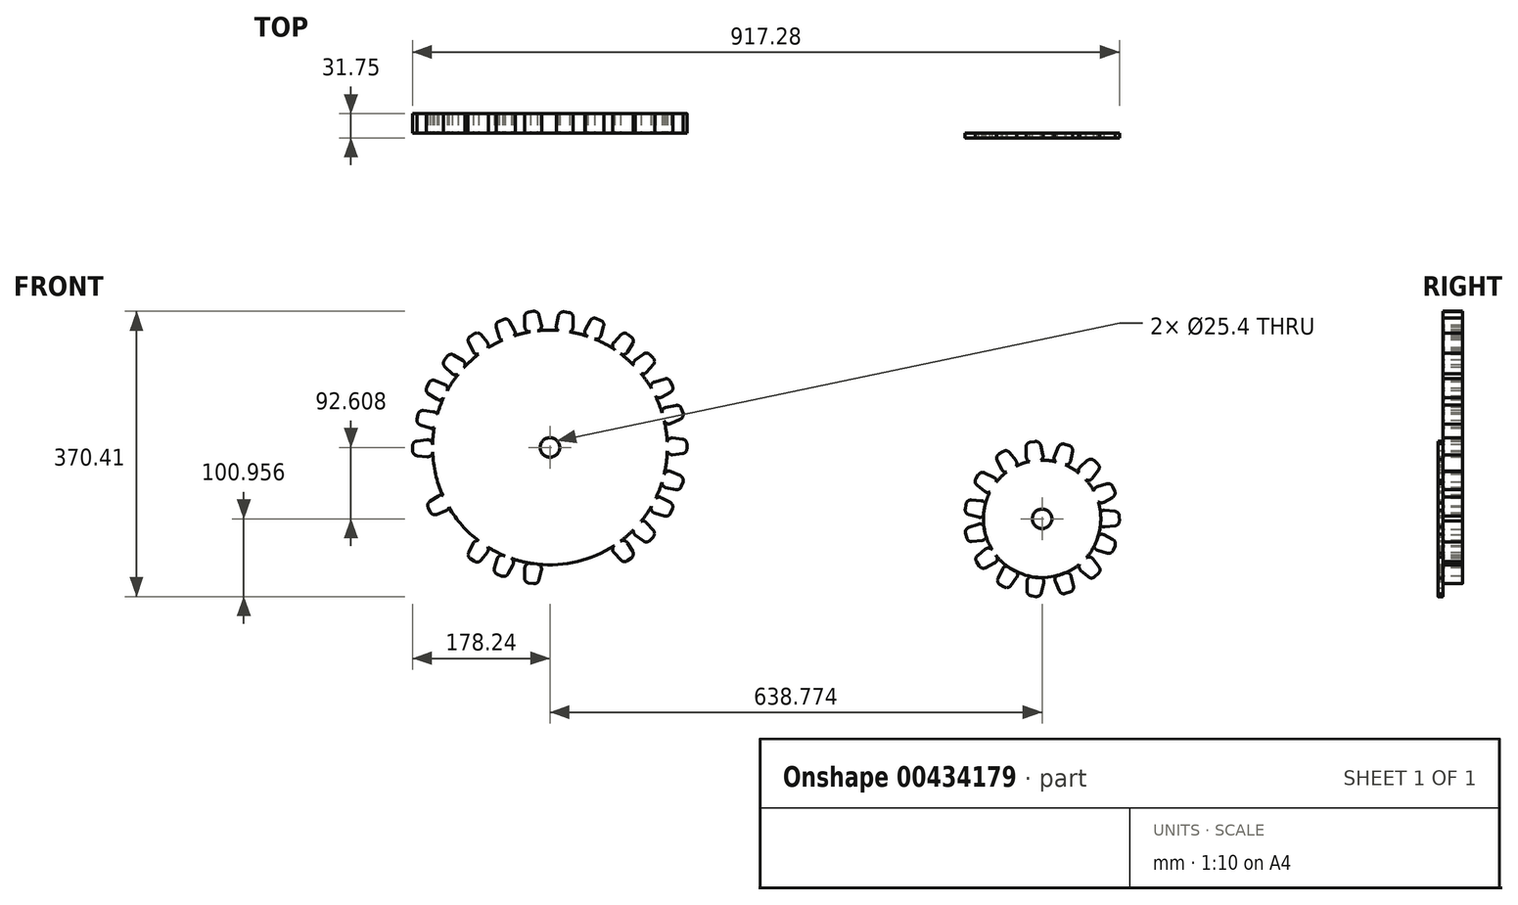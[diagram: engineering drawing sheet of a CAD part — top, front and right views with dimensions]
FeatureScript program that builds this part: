
annotation { "Feature Type Name" : "Feature", "Feature Type Description" : "" }
export const myFeature = defineFeature(function(context is Context, id is Id, definition is map)
    precondition{}
    {
        {
            var Q0;
            Q0=qCreatedBy(makeId("Front.planeOp"),FACE);
            var sketch = newSketch(context, id + "F0", { "sketchPlane" : qUnion([Q0])});
            skCircle(sketch, "E0", {"center": v(-249.13, 151.4) * mm, "radius": 152.4 * mm});
            skCircle(sketch, "E1", {"center": v(-249.13, 151.4) * mm, "radius": 12.7 * mm});
            skLineSegment(sketch, "E2", {"start": v(-197.07, 316) * mm, "end": v(-203.37, 304.29) * mm});
            skLineSegment(sketch, "E3", {"start": v(-199.76, 295.58) * mm, "end": v(-191.3, 292.4) * mm});
            skLineSegment(sketch, "E4", {"start": v(-183.23, 316.56) * mm, "end": v(-189.13, 318.9) * mm});
            skLineSegment(sketch, "E5.MirrorCS", {"start": v(-179.48, 308.88) * mm, "end": v(-183.09, 296.5) * mm});
            skArc(sketch, "E6.filletArc", {"start": v(-203.37, 304.29) * mm, "mid": v(-203.45, 299.15) * mm, "end": v(-199.76, 295.58) * mm});
            skArc(sketch, "E7.filletArc", {"start": v(-191.3, 292.4) * mm, "mid": v(-186.3, 292.65) * mm, "end": v(-183.09, 296.5) * mm});
            skArc(sketch, "E8.filletArc", {"start": v(-189.13, 318.9) * mm, "mid": v(-193.65, 318.96) * mm, "end": v(-197.07, 316) * mm});
            skPoint(sketch, "E9.newPointA", {"position": v(-185.74, 317.55) * mm});
            skArc(sketch, "E9.filletArc", {"start": v(-179.48, 308.88) * mm, "mid": v(-179.87, 313.44) * mm, "end": v(-183.23, 316.56) * mm});
            skLineSegment(sketch, "E10", {"start": v(-237.85, 322.67) * mm, "end": v(-240.9, 309.72) * mm});
            skLineSegment(sketch, "E11", {"start": v(-235.44, 302.37) * mm, "end": v(-226.34, 301.2) * mm});
            skLineSegment(sketch, "E12", {"start": v(-224.63, 326.78) * mm, "end": v(-230.94, 327.52) * mm});
            skLineSegment(sketch, "E13.MirrorCS", {"start": v(-219.02, 320.33) * mm, "end": v(-219.3, 307.27) * mm});
            skArc(sketch, "E14.filletArc", {"start": v(-240.9, 309.72) * mm, "mid": v(-239.74, 304.88) * mm, "end": v(-235.44, 302.37) * mm});
            skArc(sketch, "E15.filletArc", {"start": v(-226.34, 301.2) * mm, "mid": v(-221.47, 302.67) * mm, "end": v(-219.3, 307.27) * mm});
            skArc(sketch, "E16.filletArc", {"start": v(-230.94, 327.52) * mm, "mid": v(-235.32, 326.4) * mm, "end": v(-237.85, 322.67) * mm});
            skPoint(sketch, "E17.newPointA", {"position": v(-225.8, 326.92) * mm});
            skArc(sketch, "E17.filletArc", {"start": v(-219.02, 320.33) * mm, "mid": v(-220.57, 324.64) * mm, "end": v(-224.63, 326.78) * mm});
            skLineSegment(sketch, "E18", {"start": v(-282.04, 320.78) * mm, "end": v(-281.63, 307.48) * mm});
            skLineSegment(sketch, "E19", {"start": v(-274.3, 301.7) * mm, "end": v(-265.32, 302.93) * mm});
            skLineSegment(sketch, "E20", {"start": v(-270.33, 328.18) * mm, "end": v(-276.61, 327.25) * mm});
            skLineSegment(sketch, "E21.MirrorCS", {"start": v(-263.24, 323.4) * mm, "end": v(-260.1, 310.6) * mm});
            skArc(sketch, "E22.filletArc", {"start": v(-281.63, 307.48) * mm, "mid": v(-279.19, 303.03) * mm, "end": v(-274.3, 301.7) * mm});
            skArc(sketch, "E23.filletArc", {"start": v(-265.32, 302.93) * mm, "mid": v(-261.01, 305.6) * mm, "end": v(-260.1, 310.6) * mm});
            skArc(sketch, "E24.filletArc", {"start": v(-276.61, 327.25) * mm, "mid": v(-280.56, 325.05) * mm, "end": v(-282.04, 320.78) * mm});
            skPoint(sketch, "E25.newPointA", {"position": v(-273, 327.78) * mm});
            skArc(sketch, "E25.filletArc", {"start": v(-263.24, 323.4) * mm, "mid": v(-265.86, 327.16) * mm, "end": v(-270.33, 328.18) * mm});
            skLineSegment(sketch, "E26", {"start": v(-318.81, 307.48) * mm, "end": v(-314.98, 294.74) * mm});
            skLineSegment(sketch, "E27", {"start": v(-306.54, 291) * mm, "end": v(-298.16, 294.5) * mm});
            skLineSegment(sketch, "E28", {"start": v(-309.42, 317.65) * mm, "end": v(-315.25, 315.14) * mm});
            skLineSegment(sketch, "E29.MirrorCS", {"start": v(-301.34, 314.88) * mm, "end": v(-295.05, 303.42) * mm});
            skArc(sketch, "E30.filletArc", {"start": v(-314.98, 294.74) * mm, "mid": v(-311.57, 291.05) * mm, "end": v(-306.54, 291) * mm});
            skArc(sketch, "E31.filletArc", {"start": v(-298.16, 294.5) * mm, "mid": v(-294.62, 298.27) * mm, "end": v(-295.05, 303.42) * mm});
            skArc(sketch, "E32.filletArc", {"start": v(-315.25, 315.14) * mm, "mid": v(-318.5, 311.99) * mm, "end": v(-318.81, 307.48) * mm});
            skPoint(sketch, "E33.newPointA", {"position": v(-311.9, 316.59) * mm});
            skArc(sketch, "E33.filletArc", {"start": v(-301.34, 314.88) * mm, "mid": v(-304.84, 317.83) * mm, "end": v(-309.42, 317.65) * mm});
            skLineSegment(sketch, "E34", {"start": v(-354.62, 287.49) * mm, "end": v(-348.63, 275.6) * mm});
            skLineSegment(sketch, "E35", {"start": v(-339.67, 273.39) * mm, "end": v(-332.03, 278.3) * mm});
            skLineSegment(sketch, "E36", {"start": v(-347.13, 299.14) * mm, "end": v(-352.44, 295.65) * mm});
            skLineSegment(sketch, "E37.MirrorCS", {"start": v(-338.69, 297.81) * mm, "end": v(-330.51, 287.62) * mm});
            skArc(sketch, "E38.filletArc", {"start": v(-348.63, 275.6) * mm, "mid": v(-344.63, 272.57) * mm, "end": v(-339.67, 273.39) * mm});
            skArc(sketch, "E39.filletArc", {"start": v(-332.03, 278.3) * mm, "mid": v(-329.2, 282.62) * mm, "end": v(-330.51, 287.62) * mm});
            skArc(sketch, "E40.filletArc", {"start": v(-352.44, 295.65) * mm, "mid": v(-355.08, 291.99) * mm, "end": v(-354.62, 287.49) * mm});
            skPoint(sketch, "E41.newPointA", {"position": v(-349.39, 297.66) * mm});
            skArc(sketch, "E41.filletArc", {"start": v(-338.69, 297.81) * mm, "mid": v(-342.65, 300.1) * mm, "end": v(-347.13, 299.14) * mm});
            skLineSegment(sketch, "E42", {"start": v(-127.84, 272.83) * mm, "end": v(-138.5, 264.88) * mm});
            skLineSegment(sketch, "E43", {"start": v(-139.13, 255.66) * mm, "end": v(-132.97, 249) * mm});
            skLineSegment(sketch, "E44", {"start": v(-115.07, 267.49) * mm, "end": v(-119.42, 272.1) * mm});
            skLineSegment(sketch, "E45.MirrorCS", {"start": v(-114.9, 258.94) * mm, "end": v(-123.53, 249.12) * mm});
            skArc(sketch, "E46.filletArc", {"start": v(-138.5, 264.88) * mm, "mid": v(-140.8, 260.4) * mm, "end": v(-139.13, 255.66) * mm});
            skArc(sketch, "E47.filletArc", {"start": v(-132.97, 249) * mm, "mid": v(-128.22, 246.95) * mm, "end": v(-123.53, 249.12) * mm});
            skArc(sketch, "E48.filletArc", {"start": v(-119.42, 272.1) * mm, "mid": v(-123.5, 274.07) * mm, "end": v(-127.84, 272.83) * mm});
            skPoint(sketch, "E49.newPointA", {"position": v(-116.92, 269.45) * mm});
            skArc(sketch, "E49.filletArc", {"start": v(-114.9, 258.94) * mm, "mid": v(-113.33, 263.24) * mm, "end": v(-115.07, 267.49) * mm});
            skLineSegment(sketch, "E50", {"start": v(-385.37, 256.27) * mm, "end": v(-375.68, 247.15) * mm});
            skLineSegment(sketch, "E51", {"start": v(-366.65, 247.94) * mm, "end": v(-360.51, 255.4) * mm});
            skLineSegment(sketch, "E52", {"start": v(-382.33, 269.78) * mm, "end": v(-386.12, 264.68) * mm});
            skLineSegment(sketch, "E53.MirrorCS", {"start": v(-373.94, 271.42) * mm, "end": v(-362, 264.17) * mm});
            skArc(sketch, "E54.filletArc", {"start": v(-375.68, 247.15) * mm, "mid": v(-371, 245.65) * mm, "end": v(-366.65, 247.94) * mm});
            skArc(sketch, "E55.filletArc", {"start": v(-360.51, 255.4) * mm, "mid": v(-359.26, 260.13) * mm, "end": v(-362, 264.17) * mm});
            skArc(sketch, "E56.filletArc", {"start": v(-386.12, 264.68) * mm, "mid": v(-387.35, 260.34) * mm, "end": v(-385.37, 256.27) * mm});
            skPoint(sketch, "E57.newPointA", {"position": v(-383.94, 267.61) * mm});
            skArc(sketch, "E57.filletArc", {"start": v(-373.94, 271.42) * mm, "mid": v(-378.45, 272.22) * mm, "end": v(-382.33, 269.78) * mm});
            skLineSegment(sketch, "E58", {"start": v(-156.92, 297.77) * mm, "end": v(-166.04, 288.08) * mm});
            skLineSegment(sketch, "E59", {"start": v(-165.06, 278.5) * mm, "end": v(-157.65, 273.27) * mm});
            skLineSegment(sketch, "E60", {"start": v(-143.41, 294.72) * mm, "end": v(-148.5, 298.5) * mm});
            skLineSegment(sketch, "E61.MirrorCS", {"start": v(-141.77, 286.33) * mm, "end": v(-148.56, 275.16) * mm});
            skArc(sketch, "E62.filletArc", {"start": v(-166.04, 288.08) * mm, "mid": v(-167.73, 283.07) * mm, "end": v(-165.06, 278.5) * mm});
            skArc(sketch, "E63.filletArc", {"start": v(-157.65, 273.27) * mm, "mid": v(-152.7, 272.23) * mm, "end": v(-148.56, 275.16) * mm});
            skArc(sketch, "E64.filletArc", {"start": v(-148.5, 298.5) * mm, "mid": v(-152.85, 299.74) * mm, "end": v(-156.92, 297.77) * mm});
            skPoint(sketch, "E65.newPointA", {"position": v(-145.58, 296.33) * mm});
            skArc(sketch, "E65.filletArc", {"start": v(-141.77, 286.33) * mm, "mid": v(-140.97, 290.84) * mm, "end": v(-143.41, 294.72) * mm});
            skLineSegment(sketch, "E66", {"start": v(-100.26, 240.41) * mm, "end": v(-113, 236.58) * mm});
            skLineSegment(sketch, "E67", {"start": v(-117.37, 227.99) * mm, "end": v(-113.04, 219.37) * mm});
            skLineSegment(sketch, "E68", {"start": v(-90.08, 231.02) * mm, "end": v(-92.6, 236.85) * mm});
            skLineSegment(sketch, "E69.MirrorCS", {"start": v(-92.86, 222.94) * mm, "end": v(-104.32, 216.65) * mm});
            skArc(sketch, "E70.filletArc", {"start": v(-113, 236.58) * mm, "mid": v(-117.36, 233.4) * mm, "end": v(-117.37, 227.99) * mm});
            skArc(sketch, "E71.filletArc", {"start": v(-113.04, 219.37) * mm, "mid": v(-109.26, 216.16) * mm, "end": v(-104.32, 216.65) * mm});
            skArc(sketch, "E72.filletArc", {"start": v(-92.6, 236.85) * mm, "mid": v(-95.75, 240.1) * mm, "end": v(-100.26, 240.41) * mm});
            skPoint(sketch, "E73.newPointA", {"position": v(-91.15, 233.5) * mm});
            skArc(sketch, "E73.filletArc", {"start": v(-92.86, 222.94) * mm, "mid": v(-89.9, 226.44) * mm, "end": v(-90.08, 231.02) * mm});
            skLineSegment(sketch, "E74", {"start": v(-85.84, 206.07) * mm, "end": v(-98.86, 203.37) * mm});
            skLineSegment(sketch, "E75", {"start": v(-103.39, 195.49) * mm, "end": v(-100.8, 186.34) * mm});
            skLineSegment(sketch, "E76", {"start": v(-76.52, 195.83) * mm, "end": v(-78.52, 201.86) * mm});
            skLineSegment(sketch, "E77.MirrorCS", {"start": v(-80, 188.02) * mm, "end": v(-92.59, 182.48) * mm});
            skArc(sketch, "E78.filletArc", {"start": v(-98.86, 203.37) * mm, "mid": v(-102.79, 200.38) * mm, "end": v(-103.39, 195.49) * mm});
            skArc(sketch, "E79.filletArc", {"start": v(-100.8, 186.34) * mm, "mid": v(-97.57, 182.54) * mm, "end": v(-92.59, 182.48) * mm});
            skArc(sketch, "E80.filletArc", {"start": v(-78.52, 201.86) * mm, "mid": v(-81.37, 205.36) * mm, "end": v(-85.84, 206.07) * mm});
            skPoint(sketch, "E81.newPointA", {"position": v(-77.37, 198.4) * mm});
            skArc(sketch, "E81.filletArc", {"start": v(-80, 188.02) * mm, "mid": v(-76.74, 191.25) * mm, "end": v(-76.52, 195.83) * mm});
            skLineSegment(sketch, "E82", {"start": v(-406.94, 221.4) * mm, "end": v(-395.82, 214.1) * mm});
            skLineSegment(sketch, "E83", {"start": v(-386.82, 216.53) * mm, "end": v(-382.58, 225) * mm});
            skLineSegment(sketch, "E84", {"start": v(-406.29, 235.22) * mm, "end": v(-409.14, 229.55) * mm});
            skLineSegment(sketch, "E85.MirrorCS", {"start": v(-398.31, 238.3) * mm, "end": v(-385.83, 233.44) * mm});
            skArc(sketch, "E86.filletArc", {"start": v(-395.82, 214.1) * mm, "mid": v(-390.77, 213.3) * mm, "end": v(-386.82, 216.53) * mm});
            skArc(sketch, "E87.filletArc", {"start": v(-382.58, 225) * mm, "mid": v(-382.34, 229.94) * mm, "end": v(-385.83, 233.44) * mm});
            skArc(sketch, "E88.filletArc", {"start": v(-409.14, 229.55) * mm, "mid": v(-409.6, 225.05) * mm, "end": v(-406.94, 221.4) * mm});
            skPoint(sketch, "E89.newPointA", {"position": v(-407.5, 232.81) * mm});
            skArc(sketch, "E89.filletArc", {"start": v(-398.31, 238.3) * mm, "mid": v(-402.9, 238.3) * mm, "end": v(-406.29, 235.22) * mm});
            skLineSegment(sketch, "E90", {"start": v(-417.45, 180.72) * mm, "end": v(-404.81, 176.55) * mm});
            skLineSegment(sketch, "E91", {"start": v(-396.9, 181.32) * mm, "end": v(-394.98, 190.2) * mm});
            skLineSegment(sketch, "E92", {"start": v(-420.4, 194.25) * mm, "end": v(-421.68, 188.03) * mm});
            skLineSegment(sketch, "E93.MirrorCS", {"start": v(-413.48, 199.28) * mm, "end": v(-400.5, 197.85) * mm});
            skArc(sketch, "E94.filletArc", {"start": v(-404.81, 176.55) * mm, "mid": v(-399.83, 177.23) * mm, "end": v(-396.9, 181.32) * mm});
            skArc(sketch, "E95.filletArc", {"start": v(-394.98, 190.2) * mm, "mid": v(-396.03, 195.25) * mm, "end": v(-400.5, 197.85) * mm});
            skArc(sketch, "E96.filletArc", {"start": v(-421.68, 188.03) * mm, "mid": v(-420.95, 183.57) * mm, "end": v(-417.45, 180.72) * mm});
            skPoint(sketch, "E97.newPointA", {"position": v(-420.94, 191.6) * mm});
            skArc(sketch, "E97.filletArc", {"start": v(-413.48, 199.28) * mm, "mid": v(-417.91, 198.1) * mm, "end": v(-420.4, 194.25) * mm});
            skLineSegment(sketch, "E98.MirrorCS", {"start": v(-115.07, 35.3) * mm, "end": v(-119.42, 30.68) * mm});
            skLineSegment(sketch, "E99.MirrorCS", {"start": v(-143.41, 8.07) * mm, "end": v(-148.5, 4.28) * mm});
            skLineSegment(sketch, "E100.MirrorCS", {"start": v(-90.08, 71.77) * mm, "end": v(-92.6, 65.94) * mm});
            skArc(sketch, "E101.MirrorCS", {"start": v(-227, 0.6) * mm, "mid": v(-222.04, -0.95) * mm, "end": v(-219.9, -5.7) * mm});
            skLineSegment(sketch, "E102.MirrorCS", {"start": v(-200.04, 7.12) * mm, "end": v(-191.64, 10.56) * mm});
            skLineSegment(sketch, "E103.MirrorCS", {"start": v(-139.13, 47.12) * mm, "end": v(-132.97, 53.8) * mm});
            skLineSegment(sketch, "E104.MirrorCS", {"start": v(-156.92, 5.02) * mm, "end": v(-166.04, 14.71) * mm});
            skLineSegment(sketch, "E105.MirrorCS", {"start": v(-236.16, -0.45) * mm, "end": v(-227, 0.6) * mm});
            skArc(sketch, "E106.MirrorCS", {"start": v(-179.48, -6.1) * mm, "mid": v(-179.87, -10.66) * mm, "end": v(-183.23, -13.77) * mm});
            skArc(sketch, "E107.MirrorCS", {"start": v(-92.6, 65.94) * mm, "mid": v(-95.75, 62.7) * mm, "end": v(-100.26, 62.37) * mm});
            skLineSegment(sketch, "E108.MirrorCS", {"start": v(-225.23, -25.2) * mm, "end": v(-231.54, -25.94) * mm});
            skLineSegment(sketch, "E109.MirrorCS", {"start": v(-127.84, 29.95) * mm, "end": v(-138.5, 37.91) * mm});
            skLineSegment(sketch, "E110.MirrorCS", {"start": v(-76.52, 106.96) * mm, "end": v(-78.52, 100.93) * mm});
            skLineSegment(sketch, "E111.MirrorCS", {"start": v(-114.9, 43.85) * mm, "end": v(-123.53, 53.67) * mm});
            skLineSegment(sketch, "E112.MirrorCS", {"start": v(-141.77, 16.46) * mm, "end": v(-148.56, 27.63) * mm});
            skLineSegment(sketch, "E113.MirrorCS", {"start": v(-117.31, 74.9) * mm, "end": v(-113.23, 83.02) * mm});
            skArc(sketch, "E114.MirrorCS", {"start": v(-241.5, -8.14) * mm, "mid": v(-240.53, -3.12) * mm, "end": v(-236.16, -0.45) * mm});
            skArc(sketch, "E115.MirrorCS", {"start": v(-98.86, 99.42) * mm, "mid": v(-102.84, 102.5) * mm, "end": v(-103.33, 107.5) * mm});
            skArc(sketch, "E116.MirrorCS", {"start": v(-166.04, 14.71) * mm, "mid": v(-167.8, 19.38) * mm, "end": v(-165.66, 23.89) * mm});
            skArc(sketch, "E117.MirrorCS", {"start": v(-138.5, 37.91) * mm, "mid": v(-140.8, 42.38) * mm, "end": v(-139.13, 47.12) * mm});
            skArc(sketch, "E118.MirrorCS", {"start": v(-92.86, 79.85) * mm, "mid": v(-89.9, 76.35) * mm, "end": v(-90.08, 71.77) * mm});
            skArc(sketch, "E119.MirrorCS", {"start": v(-114.9, 43.85) * mm, "mid": v(-113.33, 39.54) * mm, "end": v(-115.07, 35.3) * mm});
            skArc(sketch, "E120.MirrorCS", {"start": v(-141.77, 16.46) * mm, "mid": v(-140.97, 11.95) * mm, "end": v(-143.41, 8.07) * mm});
            skArc(sketch, "E121.MirrorCS", {"start": v(-80, 114.77) * mm, "mid": v(-76.74, 111.54) * mm, "end": v(-76.52, 106.96) * mm});
            skArc(sketch, "E122.MirrorCS", {"start": v(-219.62, -18.76) * mm, "mid": v(-221.18, -23.07) * mm, "end": v(-225.23, -25.2) * mm});
            skArc(sketch, "E123.MirrorCS", {"start": v(-119.42, 30.68) * mm, "mid": v(-123.5, 28.72) * mm, "end": v(-127.84, 29.95) * mm});
            skArc(sketch, "E124.MirrorCS", {"start": v(-148.5, 4.28) * mm, "mid": v(-152.85, 3.05) * mm, "end": v(-156.92, 5.02) * mm});
            skArc(sketch, "E125.MirrorCS", {"start": v(-78.52, 100.93) * mm, "mid": v(-81.37, 97.43) * mm, "end": v(-85.84, 96.71) * mm});
            skArc(sketch, "E126.MirrorCS", {"start": v(-231.54, -25.94) * mm, "mid": v(-235.92, -24.83) * mm, "end": v(-238.46, -21.09) * mm});
            skArc(sketch, "E127.MirrorCS", {"start": v(-132.97, 53.8) * mm, "mid": v(-128.22, 55.83) * mm, "end": v(-123.53, 53.67) * mm});
            skLineSegment(sketch, "E128.MirrorCS", {"start": v(-183.23, -13.77) * mm, "end": v(-189.13, -16.11) * mm});
            skArc(sketch, "E129.MirrorCS", {"start": v(-100.84, 116.26) * mm, "mid": v(-97.26, 120.19) * mm, "end": v(-91.95, 120.03) * mm});
            skArc(sketch, "E130.MirrorCS", {"start": v(-157.83, 29.4) * mm, "mid": v(-152.8, 30.58) * mm, "end": v(-148.56, 27.63) * mm});
            skArc(sketch, "E131.MirrorCS", {"start": v(-113.23, 83.02) * mm, "mid": v(-109.46, 86.56) * mm, "end": v(-104.32, 86.14) * mm});
            skLineSegment(sketch, "E132.MirrorCS", {"start": v(-165.66, 23.89) * mm, "end": v(-157.83, 29.4) * mm});
            skArc(sketch, "E133.MirrorCS", {"start": v(-189.13, -16.11) * mm, "mid": v(-193.65, -16.18) * mm, "end": v(-197.07, -13.22) * mm});
            skLineSegment(sketch, "E134.MirrorCS", {"start": v(-92.86, 79.85) * mm, "end": v(-104.32, 86.14) * mm});
            skArc(sketch, "E135.MirrorCS", {"start": v(-191.64, 10.56) * mm, "mid": v(-186.48, 10.4) * mm, "end": v(-183.14, 6.46) * mm});
            skArc(sketch, "E136.MirrorCS", {"start": v(-113, 66.2) * mm, "mid": v(-117.18, 69.55) * mm, "end": v(-117.31, 74.9) * mm});
            skArc(sketch, "E137.MirrorCS", {"start": v(-203.37, -1.5) * mm, "mid": v(-203.56, 3.53) * mm, "end": v(-200.04, 7.12) * mm});
            skLineSegment(sketch, "E138.MirrorCS", {"start": v(-103.33, 107.5) * mm, "end": v(-100.84, 116.26) * mm});
            skPoint(sketch, "E139.MirrorP", {"position": v(-91.15, 69.29) * mm});
            skLineSegment(sketch, "E140.MirrorCS", {"start": v(-197.07, -13.22) * mm, "end": v(-203.37, -1.5) * mm});
            skPoint(sketch, "E141.MirrorP", {"position": v(-145.58, 6.46) * mm});
            skLineSegment(sketch, "E142.MirrorCS", {"start": v(-219.62, -18.76) * mm, "end": v(-219.9, -5.7) * mm});
            skLineSegment(sketch, "E143.MirrorCS", {"start": v(-80, 114.77) * mm, "end": v(-91.95, 120.03) * mm});
            skLineSegment(sketch, "E144.MirrorCS", {"start": v(-238.46, -21.09) * mm, "end": v(-241.5, -8.14) * mm});
            skPoint(sketch, "E145.MirrorP", {"position": v(-226.4, -25.34) * mm});
            skLineSegment(sketch, "E146.MirrorCS", {"start": v(-100.26, 62.37) * mm, "end": v(-113, 66.2) * mm});
            skPoint(sketch, "E147.MirrorP", {"position": v(-185.74, -14.77) * mm});
            skPoint(sketch, "E148.MirrorP", {"position": v(-116.92, 33.34) * mm});
            skPoint(sketch, "E149.MirrorP", {"position": v(-77.37, 104.4) * mm});
            skLineSegment(sketch, "E150.MirrorCS", {"start": v(-179.48, -6.1) * mm, "end": v(-183.14, 6.46) * mm});
            skLineSegment(sketch, "E151.MirrorCS", {"start": v(-85.84, 96.71) * mm, "end": v(-98.86, 99.42) * mm});
            skLineSegment(sketch, "E152.MirrorCS", {"start": v(-311.78, -15.52) * mm, "end": v(-317.61, -13) * mm});
            skArc(sketch, "E153.MirrorCS", {"start": v(-413, 103.11) * mm, "mid": v(-417.44, 104.29) * mm, "end": v(-419.92, 108.14) * mm});
            skArc(sketch, "E154.MirrorCS", {"start": v(-372.47, 32.35) * mm, "mid": v(-376.98, 31.55) * mm, "end": v(-380.86, 33.99) * mm});
            skLineSegment(sketch, "E155.MirrorCS", {"start": v(-380.86, 33.99) * mm, "end": v(-384.65, 39.08) * mm});
            skLineSegment(sketch, "E156.MirrorCS", {"start": v(-347.13, 3.65) * mm, "end": v(-352.44, 7.14) * mm});
            skLineSegment(sketch, "E157.MirrorCS", {"start": v(-404.23, 67.56) * mm, "end": v(-407.08, 73.24) * mm});
            skArc(sketch, "E158.MirrorCS", {"start": v(-396.25, 64.5) * mm, "mid": v(-400.84, 64.48) * mm, "end": v(-404.23, 67.56) * mm});
            skArc(sketch, "E159.MirrorCS", {"start": v(-276.61, -24.47) * mm, "mid": v(-280.56, -22.26) * mm, "end": v(-282.04, -18) * mm});
            skLineSegment(sketch, "E160.MirrorCS", {"start": v(-419.92, 108.14) * mm, "end": v(-421.2, 114.36) * mm});
            skArc(sketch, "E161.MirrorCS", {"start": v(-303.7, -12.74) * mm, "mid": v(-307.2, -15.7) * mm, "end": v(-311.78, -15.52) * mm});
            skLineSegment(sketch, "E162.MirrorCS", {"start": v(-282.04, -18) * mm, "end": v(-281.63, -4.7) * mm});
            skLineSegment(sketch, "E163.MirrorCS", {"start": v(-383.9, 47.5) * mm, "end": v(-374.22, 56.61) * mm});
            skLineSegment(sketch, "E164.MirrorCS", {"start": v(-354.62, 15.3) * mm, "end": v(-348.63, 27.18) * mm});
            skArc(sketch, "E165.MirrorCS", {"start": v(-359.54, 48.4) * mm, "mid": v(-358.35, 43.38) * mm, "end": v(-361.3, 39.13) * mm});
            skArc(sketch, "E166.MirrorCS", {"start": v(-265.2, -0.16) * mm, "mid": v(-260.98, -2.94) * mm, "end": v(-260.14, -7.92) * mm});
            skLineSegment(sketch, "E167.MirrorCS", {"start": v(-274.45, 1.1) * mm, "end": v(-265.2, -0.16) * mm});
            skArc(sketch, "E168.MirrorCS", {"start": v(-393.76, 88.7) * mm, "mid": v(-388.77, 89.32) * mm, "end": v(-384.9, 86.13) * mm});
            skArc(sketch, "E169.MirrorCS", {"start": v(-281.63, -4.7) * mm, "mid": v(-279.29, -0.24) * mm, "end": v(-274.45, 1.1) * mm});
            skArc(sketch, "E170.MirrorCS", {"start": v(-348.63, 27.18) * mm, "mid": v(-344.63, 30.22) * mm, "end": v(-339.67, 29.4) * mm});
            skLineSegment(sketch, "E171.MirrorCS", {"start": v(-396.25, 64.5) * mm, "end": v(-384.07, 69.23) * mm});
            skLineSegment(sketch, "E172.MirrorCS", {"start": v(-339.67, 29.4) * mm, "end": v(-332.03, 24.49) * mm});
            skLineSegment(sketch, "E173.MirrorCS", {"start": v(-404.89, 81.4) * mm, "end": v(-393.76, 88.7) * mm});
            skArc(sketch, "E174.MirrorCS", {"start": v(-380.73, 78.06) * mm, "mid": v(-380.44, 72.9) * mm, "end": v(-384.07, 69.23) * mm});
            skArc(sketch, "E175.MirrorCS", {"start": v(-332.03, 24.49) * mm, "mid": v(-329.2, 20.17) * mm, "end": v(-330.51, 15.17) * mm});
            skArc(sketch, "E176.MirrorCS", {"start": v(-338.69, 4.98) * mm, "mid": v(-342.65, 2.68) * mm, "end": v(-347.13, 3.65) * mm});
            skLineSegment(sketch, "E177.MirrorCS", {"start": v(-416.97, 121.67) * mm, "end": v(-404.34, 125.84) * mm});
            skLineSegment(sketch, "E178.MirrorCS", {"start": v(-338.69, 4.98) * mm, "end": v(-330.51, 15.17) * mm});
            skLineSegment(sketch, "E179.MirrorCS", {"start": v(-263.24, -20.61) * mm, "end": v(-260.14, -7.92) * mm});
            skLineSegment(sketch, "E180.MirrorCS", {"start": v(-372.47, 32.35) * mm, "end": v(-361.3, 39.13) * mm});
            skArc(sketch, "E181.MirrorCS", {"start": v(-384.65, 39.08) * mm, "mid": v(-385.88, 43.43) * mm, "end": v(-383.9, 47.5) * mm});
            skArc(sketch, "E182.MirrorCS", {"start": v(-352.44, 7.14) * mm, "mid": v(-355.08, 10.8) * mm, "end": v(-354.62, 15.3) * mm});
            skArc(sketch, "E183.MirrorCS", {"start": v(-407.08, 73.24) * mm, "mid": v(-407.54, 77.73) * mm, "end": v(-404.89, 81.4) * mm});
            skLineSegment(sketch, "E184.MirrorCS", {"start": v(-308.9, 11.14) * mm, "end": v(-299.27, 7.48) * mm});
            skLineSegment(sketch, "E185.MirrorCS", {"start": v(-396.43, 121.07) * mm, "end": v(-394.5, 112.2) * mm});
            skLineSegment(sketch, "E186.MirrorCS", {"start": v(-303.7, -12.74) * mm, "end": v(-297.41, -1.28) * mm});
            skLineSegment(sketch, "E187.MirrorCS", {"start": v(-413, 103.11) * mm, "end": v(-400.02, 104.54) * mm});
            skArc(sketch, "E188.MirrorCS", {"start": v(-299.27, 7.48) * mm, "mid": v(-296.53, 3.48) * mm, "end": v(-297.41, -1.28) * mm});
            skLineSegment(sketch, "E189.MirrorCS", {"start": v(-384.9, 86.13) * mm, "end": v(-380.73, 78.06) * mm});
            skLineSegment(sketch, "E190.MirrorCS", {"start": v(-321.18, -5.34) * mm, "end": v(-317.34, 7.4) * mm});
            skArc(sketch, "E191.MirrorCS", {"start": v(-421.2, 114.36) * mm, "mid": v(-420.48, 118.82) * mm, "end": v(-416.97, 121.67) * mm});
            skArc(sketch, "E192.MirrorCS", {"start": v(-317.61, -13) * mm, "mid": v(-320.85, -9.85) * mm, "end": v(-321.18, -5.34) * mm});
            skLineSegment(sketch, "E193.MirrorCS", {"start": v(-365.04, 55.63) * mm, "end": v(-359.54, 48.4) * mm});
            skArc(sketch, "E194.MirrorCS", {"start": v(-374.22, 56.61) * mm, "mid": v(-369.41, 58.1) * mm, "end": v(-365.04, 55.63) * mm});
            skArc(sketch, "E195.MirrorCS", {"start": v(-394.5, 112.2) * mm, "mid": v(-395.55, 107.14) * mm, "end": v(-400.02, 104.54) * mm});
            skArc(sketch, "E196.MirrorCS", {"start": v(-404.34, 125.84) * mm, "mid": v(-399.36, 125.16) * mm, "end": v(-396.43, 121.07) * mm});
            skArc(sketch, "E197.MirrorCS", {"start": v(-317.34, 7.4) * mm, "mid": v(-313.93, 11.09) * mm, "end": v(-308.9, 11.14) * mm});
            skPoint(sketch, "E198.MirrorP", {"position": v(-273, -25) * mm});
            skPoint(sketch, "E199.MirrorP", {"position": v(-314.26, -14.45) * mm});
            skPoint(sketch, "E200.MirrorP", {"position": v(-405.44, 69.97) * mm});
            skPoint(sketch, "E201.MirrorP", {"position": v(-382.47, 36.15) * mm});
            skPoint(sketch, "E202.MirrorP", {"position": v(-349.39, 5.13) * mm});
            skPoint(sketch, "E203.MirrorP", {"position": v(-420.46, 110.78) * mm});
            skLineSegment(sketch, "E204.MirrorCS", {"start": v(-270.33, -25.39) * mm, "end": v(-276.61, -24.47) * mm});
            skArc(sketch, "E205.MirrorCS", {"start": v(-265.45, -0.12) * mm, "mid": v(-261.06, -2.83) * mm, "end": v(-260.14, -7.92) * mm});
            skArc(sketch, "E206.MirrorCS", {"start": v(-263.24, -20.61) * mm, "mid": v(-265.86, -24.37) * mm, "end": v(-270.33, -25.39) * mm});
            skLineSegment(sketch, "E207.MirrorCS", {"start": v(-274.45, 1.1) * mm, "end": v(-265.45, -0.12) * mm});
            skLineSegment(sketch, "E208", {"start": v(-77.12, 162.35) * mm, "end": v(-90.35, 163.73) * mm});
            skLineSegment(sketch, "E209", {"start": v(-97.06, 157.39) * mm, "end": v(-97.05, 148.3) * mm});
            skLineSegment(sketch, "E210", {"start": v(-71.36, 149.76) * mm, "end": v(-71.43, 156.11) * mm});
            skLineSegment(sketch, "E211.MirrorCS", {"start": v(-77.04, 143.37) * mm, "end": v(-90.03, 142) * mm});
            skArc(sketch, "E212.filletArc", {"start": v(-90.35, 163.73) * mm, "mid": v(-95.07, 162) * mm, "end": v(-97.06, 157.39) * mm});
            skArc(sketch, "E213.filletArc", {"start": v(-97.05, 148.3) * mm, "mid": v(-94.95, 143.6) * mm, "end": v(-90.03, 142) * mm});
            skArc(sketch, "E214.filletArc", {"start": v(-71.43, 156.11) * mm, "mid": v(-73.09, 160.32) * mm, "end": v(-77.12, 162.35) * mm});
            skPoint(sketch, "E215.newPointA", {"position": v(-71.39, 152.46) * mm});
            skArc(sketch, "E215.filletArc", {"start": v(-77.04, 143.37) * mm, "mid": v(-72.96, 145.47) * mm, "end": v(-71.36, 149.76) * mm});
            skLineSegment(sketch, "E216", {"start": v(-421.45, 140.74) * mm, "end": v(-408.2, 139.52) * mm});
            skLineSegment(sketch, "E217", {"start": v(-401.42, 145.6) * mm, "end": v(-401.49, 154.9) * mm});
            skLineSegment(sketch, "E218", {"start": v(-427.37, 153.26) * mm, "end": v(-427.22, 146.91) * mm});
            skLineSegment(sketch, "E219.MirrorCS", {"start": v(-421.76, 159.72) * mm, "end": v(-408.7, 161.26) * mm});
            skArc(sketch, "E220.filletArc", {"start": v(-408.2, 139.52) * mm, "mid": v(-403.44, 141.03) * mm, "end": v(-401.42, 145.6) * mm});
            skArc(sketch, "E221.filletArc", {"start": v(-401.49, 154.9) * mm, "mid": v(-403.67, 159.69) * mm, "end": v(-408.7, 161.26) * mm});
            skArc(sketch, "E222.filletArc", {"start": v(-427.22, 146.91) * mm, "mid": v(-425.51, 142.73) * mm, "end": v(-421.45, 140.74) * mm});
            skPoint(sketch, "E223.newPointA", {"position": v(-427.3, 150.56) * mm});
            skArc(sketch, "E223.filletArc", {"start": v(-421.76, 159.72) * mm, "mid": v(-425.81, 157.57) * mm, "end": v(-427.37, 153.26) * mm});
            skSolve(sketch);
        }
        {
            var Q0;
            Q0=qCreatedBy(makeId("Front.planeOp"),FACE);
            var sketch = newSketch(context, id + "F1", { "sketchPlane" : qUnion([Q0])});
            skCircle(sketch, "E224", {"center": v(389.64, 58.79) * mm, "radius": 76.2 * mm});
            skCircle(sketch, "E225", {"center": v(389.64, 58.79) * mm, "radius": 12.7 * mm});
            skLineSegment(sketch, "E226", {"start": v(368.87, 151.8) * mm, "end": v(369.27, 138.5) * mm});
            skLineSegment(sketch, "E227", {"start": v(376.46, 132.7) * mm, "end": v(385.46, 133.93) * mm});
            skLineSegment(sketch, "E228", {"start": v(380.57, 159.2) * mm, "end": v(374.3, 158.28) * mm});
            skLineSegment(sketch, "E229.MirrorCS", {"start": v(387.66, 154.43) * mm, "end": v(390.77, 141.73) * mm});
            skArc(sketch, "E230.filletArc", {"start": v(369.27, 138.5) * mm, "mid": v(371.61, 134.06) * mm, "end": v(376.46, 132.7) * mm});
            skArc(sketch, "E231.filletArc", {"start": v(385.46, 133.93) * mm, "mid": v(389.85, 136.65) * mm, "end": v(390.77, 141.73) * mm});
            skArc(sketch, "E232.filletArc", {"start": v(374.3, 158.28) * mm, "mid": v(370.35, 156.08) * mm, "end": v(368.87, 151.8) * mm});
            skPoint(sketch, "E233.newPointA", {"position": v(377.9, 158.81) * mm});
            skArc(sketch, "E233.filletArc", {"start": v(387.66, 154.43) * mm, "mid": v(385.04, 158.19) * mm, "end": v(380.57, 159.2) * mm});
            skLineSegment(sketch, "E234", {"start": v(410.95, 152.24) * mm, "end": v(405.7, 140.02) * mm});
            skLineSegment(sketch, "E235", {"start": v(409.76, 131.73) * mm, "end": v(418.43, 129.03) * mm});
            skLineSegment(sketch, "E236", {"start": v(424.68, 154) * mm, "end": v(418.6, 155.82) * mm});
            skLineSegment(sketch, "E237.MirrorCS", {"start": v(429.1, 146.67) * mm, "end": v(426.54, 133.85) * mm});
            skArc(sketch, "E238.filletArc", {"start": v(405.7, 140.02) * mm, "mid": v(405.94, 135) * mm, "end": v(409.76, 131.73) * mm});
            skArc(sketch, "E239.filletArc", {"start": v(418.43, 129.03) * mm, "mid": v(423.56, 129.64) * mm, "end": v(426.54, 133.85) * mm});
            skArc(sketch, "E240.filletArc", {"start": v(418.6, 155.82) * mm, "mid": v(414.1, 155.49) * mm, "end": v(410.95, 152.24) * mm});
            skPoint(sketch, "E241.newPointA", {"position": v(422.1, 154.77) * mm});
            skArc(sketch, "E241.filletArc", {"start": v(429.1, 146.67) * mm, "mid": v(428.3, 151.19) * mm, "end": v(424.68, 154) * mm});
            skLineSegment(sketch, "E242", {"start": v(331.42, 134.58) * mm, "end": v(337.38, 122.69) * mm});
            skLineSegment(sketch, "E243", {"start": v(346.34, 120.45) * mm, "end": v(353.99, 125.34) * mm});
            skLineSegment(sketch, "E244", {"start": v(338.93, 146.22) * mm, "end": v(333.62, 142.74) * mm});
            skLineSegment(sketch, "E245.MirrorCS", {"start": v(347.37, 144.87) * mm, "end": v(355.53, 134.65) * mm});
            skArc(sketch, "E246.filletArc", {"start": v(337.38, 122.69) * mm, "mid": v(341.38, 119.64) * mm, "end": v(346.34, 120.45) * mm});
            skArc(sketch, "E247.filletArc", {"start": v(353.99, 125.34) * mm, "mid": v(356.83, 129.66) * mm, "end": v(355.53, 134.65) * mm});
            skArc(sketch, "E248.filletArc", {"start": v(333.62, 142.74) * mm, "mid": v(330.97, 139.08) * mm, "end": v(331.42, 134.58) * mm});
            skPoint(sketch, "E249.newPointA", {"position": v(336.67, 144.74) * mm});
            skArc(sketch, "E249.filletArc", {"start": v(347.37, 144.87) * mm, "mid": v(343.41, 147.17) * mm, "end": v(338.93, 146.22) * mm});
            skLineSegment(sketch, "E250", {"start": v(448.59, 134.53) * mm, "end": v(438.66, 125.68) * mm});
            skLineSegment(sketch, "E251", {"start": v(438.84, 116.45) * mm, "end": v(445.56, 110.34) * mm});
            skLineSegment(sketch, "E252", {"start": v(461.78, 130.32) * mm, "end": v(457.03, 134.54) * mm});
            skLineSegment(sketch, "E253.MirrorCS", {"start": v(462.68, 121.82) * mm, "end": v(454.95, 111.28) * mm});
            skArc(sketch, "E254.filletArc", {"start": v(438.66, 125.68) * mm, "mid": v(436.76, 121.02) * mm, "end": v(438.84, 116.45) * mm});
            skArc(sketch, "E255.filletArc", {"start": v(445.56, 110.34) * mm, "mid": v(450.46, 108.72) * mm, "end": v(454.95, 111.28) * mm});
            skArc(sketch, "E256.filletArc", {"start": v(457.03, 134.54) * mm, "mid": v(452.8, 136.15) * mm, "end": v(448.59, 134.53) * mm});
            skPoint(sketch, "E257.newPointA", {"position": v(459.76, 132.11) * mm});
            skArc(sketch, "E257.filletArc", {"start": v(462.68, 121.82) * mm, "mid": v(463.87, 126.24) * mm, "end": v(461.78, 130.32) * mm});
            skLineSegment(sketch, "E258", {"start": v(305.15, 102.34) * mm, "end": v(315.6, 94.1) * mm});
            skLineSegment(sketch, "E259", {"start": v(324.65, 95.88) * mm, "end": v(329.5, 103.56) * mm});
            skLineSegment(sketch, "E260", {"start": v(307, 116.07) * mm, "end": v(303.67, 110.66) * mm});
            skLineSegment(sketch, "E261.MirrorCS", {"start": v(315.22, 118.43) * mm, "end": v(326.94, 112.65) * mm});
            skArc(sketch, "E262.filletArc", {"start": v(315.6, 94.1) * mm, "mid": v(320.5, 93.04) * mm, "end": v(324.65, 95.88) * mm});
            skArc(sketch, "E263.filletArc", {"start": v(329.5, 103.56) * mm, "mid": v(330.24, 108.67) * mm, "end": v(326.94, 112.65) * mm});
            skArc(sketch, "E264.filletArc", {"start": v(303.67, 110.66) * mm, "mid": v(302.83, 106.22) * mm, "end": v(305.15, 102.34) * mm});
            skPoint(sketch, "E265.newPointA", {"position": v(305.59, 113.77) * mm});
            skArc(sketch, "E265.filletArc", {"start": v(315.22, 118.43) * mm, "mid": v(310.66, 118.84) * mm, "end": v(307, 116.07) * mm});
            skLineSegment(sketch, "E266", {"start": v(473.66, 104.06) * mm, "end": v(460.92, 100.23) * mm});
            skLineSegment(sketch, "E267", {"start": v(457.18, 91.79) * mm, "end": v(460.69, 83.4) * mm});
            skLineSegment(sketch, "E268", {"start": v(483.84, 94.66) * mm, "end": v(481.32, 100.5) * mm});
            skLineSegment(sketch, "E269.MirrorCS", {"start": v(481.06, 86.58) * mm, "end": v(469.6, 80.3) * mm});
            skArc(sketch, "E270.filletArc", {"start": v(460.92, 100.23) * mm, "mid": v(457.23, 96.81) * mm, "end": v(457.18, 91.79) * mm});
            skArc(sketch, "E271.filletArc", {"start": v(460.69, 83.4) * mm, "mid": v(464.45, 79.87) * mm, "end": v(469.6, 80.3) * mm});
            skArc(sketch, "E272.filletArc", {"start": v(481.32, 100.5) * mm, "mid": v(478.17, 103.74) * mm, "end": v(473.66, 104.06) * mm});
            skPoint(sketch, "E273.newPointA", {"position": v(482.77, 97.14) * mm});
            skArc(sketch, "E273.filletArc", {"start": v(481.06, 86.58) * mm, "mid": v(484.01, 90.09) * mm, "end": v(483.84, 94.66) * mm});
            skLineSegment(sketch, "E274.MirrorCS", {"start": v(484.3, 23.76) * mm, "end": v(481.86, 17.9) * mm});
            skPoint(sketch, "E275.MirrorP", {"position": v(483.26, 21.27) * mm});
            skLineSegment(sketch, "E276.MirrorCS", {"start": v(481.42, 31.81) * mm, "end": v(469.88, 37.95) * mm});
            skArc(sketch, "E277.MirrorCS", {"start": v(481.86, 17.9) * mm, "mid": v(478.75, 14.62) * mm, "end": v(474.25, 14.24) * mm});
            skArc(sketch, "E278.MirrorCS", {"start": v(481.42, 31.81) * mm, "mid": v(484.41, 28.35) * mm, "end": v(484.3, 23.76) * mm});
            skArc(sketch, "E279.MirrorCS", {"start": v(461.46, 17.9) * mm, "mid": v(457.72, 21.27) * mm, "end": v(457.6, 26.3) * mm});
            skArc(sketch, "E280.MirrorCS", {"start": v(461, 34.72) * mm, "mid": v(464.72, 38.3) * mm, "end": v(469.88, 37.95) * mm});
            skLineSegment(sketch, "E281.MirrorCS", {"start": v(474.25, 14.24) * mm, "end": v(461.46, 17.9) * mm});
            skLineSegment(sketch, "E282.MirrorCS", {"start": v(457.6, 26.3) * mm, "end": v(461, 34.72) * mm});
            skLineSegment(sketch, "E283.MirrorCS", {"start": v(308.02, -2.51) * mm, "end": v(304.62, 2.85) * mm});
            skArc(sketch, "E284.MirrorCS", {"start": v(304.62, 2.85) * mm, "mid": v(303.71, 7.28) * mm, "end": v(305.98, 11.19) * mm});
            skArc(sketch, "E285.MirrorCS", {"start": v(316.27, -4.77) * mm, "mid": v(311.7, -5.23) * mm, "end": v(308.02, -2.51) * mm});
            skLineSegment(sketch, "E286.MirrorCS", {"start": v(305.98, 11.19) * mm, "end": v(316.32, 19.56) * mm});
            skArc(sketch, "E287.MirrorCS", {"start": v(330.35, 10.29) * mm, "mid": v(331.16, 5.18) * mm, "end": v(327.9, 1.17) * mm});
            skArc(sketch, "E288.MirrorCS", {"start": v(338.22, -6.17) * mm, "mid": v(342.18, -3.07) * mm, "end": v(347.15, -3.81) * mm});
            skPoint(sketch, "E289.MirrorP", {"position": v(306.57, -0.23) * mm});
            skLineSegment(sketch, "E290.MirrorCS", {"start": v(325.4, 17.9) * mm, "end": v(330.35, 10.29) * mm});
            skArc(sketch, "E291.MirrorCS", {"start": v(316.32, 19.56) * mm, "mid": v(321.22, 20.69) * mm, "end": v(325.4, 17.9) * mm});
            skLineSegment(sketch, "E292.MirrorCS", {"start": v(316.27, -4.77) * mm, "end": v(327.9, 1.17) * mm});
            skLineSegment(sketch, "E293.MirrorCS", {"start": v(340.08, -29.68) * mm, "end": v(334.72, -26.27) * mm});
            skLineSegment(sketch, "E294.MirrorCS", {"start": v(425.93, -36.34) * mm, "end": v(419.87, -38.23) * mm});
            skLineSegment(sketch, "E295.MirrorCS", {"start": v(388.92, -37.25) * mm, "end": v(391.86, -24.52) * mm});
            skLineSegment(sketch, "E296.MirrorCS", {"start": v(347.15, -3.81) * mm, "end": v(354.86, -8.6) * mm});
            skLineSegment(sketch, "E297.MirrorCS", {"start": v(410.7, -14.26) * mm, "end": v(419.35, -11.45) * mm});
            skPoint(sketch, "E298.MirrorP", {"position": v(423.35, -37.14) * mm});
            skArc(sketch, "E299.MirrorCS", {"start": v(419.87, -38.23) * mm, "mid": v(415.36, -37.96) * mm, "end": v(412.17, -34.76) * mm});
            skArc(sketch, "E300.MirrorCS", {"start": v(334.72, -26.27) * mm, "mid": v(332.02, -22.64) * mm, "end": v(332.42, -18.14) * mm});
            skPoint(sketch, "E301.MirrorP", {"position": v(379.22, -41.76) * mm});
            skLineSegment(sketch, "E302.MirrorCS", {"start": v(317.1, -4.34) * mm, "end": v(328.74, 1.6) * mm});
            skArc(sketch, "E303.MirrorCS", {"start": v(430.24, -28.95) * mm, "mid": v(429.51, -33.48) * mm, "end": v(425.93, -36.34) * mm});
            skArc(sketch, "E304.MirrorCS", {"start": v(419.35, -11.45) * mm, "mid": v(424.48, -12) * mm, "end": v(427.52, -16.17) * mm});
            skLineSegment(sketch, "E305.MirrorCS", {"start": v(377.43, -15.68) * mm, "end": v(386.44, -16.79) * mm});
            skArc(sketch, "E306.MirrorCS", {"start": v(370.32, -21.57) * mm, "mid": v(372.6, -17.1) * mm, "end": v(377.43, -15.68) * mm});
            skArc(sketch, "E307.MirrorCS", {"start": v(354.86, -8.6) * mm, "mid": v(357.76, -12.88) * mm, "end": v(356.52, -17.9) * mm});
            skLineSegment(sketch, "E308.MirrorCS", {"start": v(348.5, -28.22) * mm, "end": v(356.52, -17.9) * mm});
            skLineSegment(sketch, "E309.MirrorCS", {"start": v(370.09, -34.87) * mm, "end": v(370.32, -21.57) * mm});
            skArc(sketch, "E310.MirrorCS", {"start": v(329.16, 11.74) * mm, "mid": v(331.44, 6.56) * mm, "end": v(328.74, 1.6) * mm});
            skLineSegment(sketch, "E311.MirrorCS", {"start": v(430.24, -28.95) * mm, "end": v(427.52, -16.17) * mm});
            skPoint(sketch, "E312.MirrorP", {"position": v(337.8, -28.23) * mm});
            skArc(sketch, "E313.MirrorCS", {"start": v(386.44, -16.79) * mm, "mid": v(390.87, -19.45) * mm, "end": v(391.86, -24.52) * mm});
            skLineSegment(sketch, "E314.MirrorCS", {"start": v(332.42, -18.14) * mm, "end": v(338.22, -6.17) * mm});
            skLineSegment(sketch, "E315.MirrorCS", {"start": v(412.17, -34.76) * mm, "end": v(406.76, -22.6) * mm});
            skArc(sketch, "E316.MirrorCS", {"start": v(348.5, -28.22) * mm, "mid": v(344.57, -30.58) * mm, "end": v(340.08, -29.68) * mm});
            skArc(sketch, "E317.MirrorCS", {"start": v(406.76, -22.6) * mm, "mid": v(406.93, -17.58) * mm, "end": v(410.7, -14.26) * mm});
            skArc(sketch, "E318.MirrorCS", {"start": v(439.53, -7.83) * mm, "mid": v(437.57, -3.2) * mm, "end": v(439.59, 1.4) * mm});
            skLineSegment(sketch, "E319.MirrorCS", {"start": v(449.57, -16.56) * mm, "end": v(439.53, -7.83) * mm});
            skLineSegment(sketch, "E320.MirrorCS", {"start": v(381.9, -42.12) * mm, "end": v(375.6, -41.28) * mm});
            skArc(sketch, "E321.MirrorCS", {"start": v(388.92, -37.25) * mm, "mid": v(386.35, -41.04) * mm, "end": v(381.9, -42.12) * mm});
            skArc(sketch, "E322.MirrorCS", {"start": v(375.6, -41.28) * mm, "mid": v(371.62, -39.12) * mm, "end": v(370.09, -34.87) * mm});
            skCircle(sketch, "E323.MirrorC", {"center": v(389.65, 58.4) * mm, "radius": 76.2 * mm});
            skLineSegment(sketch, "E324.MirrorCS", {"start": v(462.71, -12.18) * mm, "end": v(458.02, -16.46) * mm});
            skLineSegment(sketch, "E325.MirrorCS", {"start": v(439.59, 1.4) * mm, "end": v(446.23, 7.6) * mm});
            skArc(sketch, "E326.MirrorCS", {"start": v(463.5, -3.67) * mm, "mid": v(464.75, -8.07) * mm, "end": v(462.71, -12.18) * mm});
            skArc(sketch, "E327.MirrorCS", {"start": v(446.23, 7.6) * mm, "mid": v(451.11, 9.28) * mm, "end": v(455.63, 6.77) * mm});
            skLineSegment(sketch, "E328.MirrorCS", {"start": v(463.5, -3.67) * mm, "end": v(455.63, 6.77) * mm});
            skPoint(sketch, "E329.MirrorP", {"position": v(460.72, -14) * mm});
            skArc(sketch, "E330.MirrorCS", {"start": v(458.02, -16.46) * mm, "mid": v(453.82, -18.12) * mm, "end": v(449.57, -16.56) * mm});
            skLineSegment(sketch, "E331", {"start": v(294.45, 64.45) * mm, "end": v(307.25, 60.81) * mm});
            skLineSegment(sketch, "E332", {"start": v(314.95, 65.9) * mm, "end": v(316.5, 74.86) * mm});
            skLineSegment(sketch, "E333", {"start": v(290.94, 77.84) * mm, "end": v(289.92, 71.57) * mm});
            skLineSegment(sketch, "E334.MirrorCS", {"start": v(297.64, 83.16) * mm, "end": v(310.68, 82.28) * mm});
            skArc(sketch, "E335.filletArc", {"start": v(307.25, 60.81) * mm, "mid": v(312.2, 61.7) * mm, "end": v(314.95, 65.9) * mm});
            skArc(sketch, "E336.filletArc", {"start": v(316.5, 74.86) * mm, "mid": v(315.24, 79.86) * mm, "end": v(310.68, 82.28) * mm});
            skArc(sketch, "E337.filletArc", {"start": v(289.92, 71.57) * mm, "mid": v(290.83, 67.15) * mm, "end": v(294.45, 64.45) * mm});
            skPoint(sketch, "E338.newPointA", {"position": v(290.5, 75.18) * mm});
            skArc(sketch, "E338.filletArc", {"start": v(297.64, 83.16) * mm, "mid": v(293.26, 81.8) * mm, "end": v(290.94, 77.84) * mm});
            skLineSegment(sketch, "E339", {"start": v(484.08, 68.6) * mm, "end": v(470.83, 69.92) * mm});
            skLineSegment(sketch, "E340", {"start": v(464.16, 63.54) * mm, "end": v(464.22, 54.45) * mm});
            skLineSegment(sketch, "E341", {"start": v(489.9, 56.05) * mm, "end": v(489.8, 62.4) * mm});
            skLineSegment(sketch, "E342.MirrorCS", {"start": v(484.26, 49.63) * mm, "end": v(471.27, 48.18) * mm});
            skArc(sketch, "E343.filletArc", {"start": v(470.83, 69.92) * mm, "mid": v(466.12, 68.16) * mm, "end": v(464.16, 63.54) * mm});
            skArc(sketch, "E344.filletArc", {"start": v(464.22, 54.45) * mm, "mid": v(466.35, 49.75) * mm, "end": v(471.27, 48.18) * mm});
            skArc(sketch, "E345.filletArc", {"start": v(489.8, 62.4) * mm, "mid": v(488.12, 66.6) * mm, "end": v(484.08, 68.6) * mm});
            skPoint(sketch, "E346.newPointA", {"position": v(489.86, 58.75) * mm});
            skArc(sketch, "E346.filletArc", {"start": v(484.26, 49.63) * mm, "mid": v(488.33, 51.75) * mm, "end": v(489.9, 56.05) * mm});
            skLineSegment(sketch, "E347", {"start": v(298.74, 29.17) * mm, "end": v(311.96, 30.73) * mm});
            skLineSegment(sketch, "E348", {"start": v(317.1, 38.4) * mm, "end": v(315.1, 47.25) * mm});
            skLineSegment(sketch, "E349", {"start": v(290.35, 40.19) * mm, "end": v(291.82, 34) * mm});
            skLineSegment(sketch, "E350.MirrorCS", {"start": v(294.5, 47.67) * mm, "end": v(306.87, 51.87) * mm});
            skArc(sketch, "E351.filletArc", {"start": v(311.96, 30.73) * mm, "mid": v(316.18, 33.45) * mm, "end": v(317.1, 38.4) * mm});
            skArc(sketch, "E352.filletArc", {"start": v(315.1, 47.25) * mm, "mid": v(312.01, 51.4) * mm, "end": v(306.87, 51.87) * mm});
            skArc(sketch, "E353.filletArc", {"start": v(291.82, 34) * mm, "mid": v(294.36, 30.27) * mm, "end": v(298.74, 29.17) * mm});
            skPoint(sketch, "E354.newPointA", {"position": v(290.98, 37.56) * mm});
            skArc(sketch, "E354.filletArc", {"start": v(294.5, 47.67) * mm, "mid": v(290.98, 44.73) * mm, "end": v(290.35, 40.19) * mm});
            skSolve(sketch);
        }
        {
            var Q0;
            Q0=makeQuery(id+"F0.imprint","IMPRINT",FACE,{"disambiguationData":[TD([[makeQuery(id+"F0.imprint","IMPRINT",EDGE,{"derivedFrom":sQuery(id+"F0.wireOp",EDGE,"E204.MirrorCS")}),-1.0]])]});
            var Q1;
            Q1=makeQuery(id+"F0.imprint","IMPRINT",FACE,{"disambiguationData":[TD([[makeQuery(id+"F0.imprint","IMPRINT",EDGE,{"derivedFrom":sQuery(id+"F0.wireOp",EDGE,"E152.MirrorCS")}),-1.0]])]});
            var Q2;
            Q2=makeQuery(id+"F0.imprint","IMPRINT",FACE,{"disambiguationData":[TD([[makeQuery(id+"F0.imprint","IMPRINT",EDGE,{"derivedFrom":sQuery(id+"F0.wireOp",EDGE,"E156.MirrorCS")}),-1.0]])]});
            var Q3;
            Q3=makeQuery(id+"F0.imprint","IMPRINT",FACE,{"disambiguationData":[TD([[makeQuery(id+"F0.imprint","IMPRINT",EDGE,{"derivedFrom":sQuery(id+"F0.wireOp",EDGE,"E154.MirrorCS")}),-1.0]])]});
            var Q4;
            Q4=makeQuery(id+"F0.imprint","IMPRINT",FACE,{"disambiguationData":[TD([[makeQuery(id+"F0.imprint","IMPRINT",EDGE,{"derivedFrom":sQuery(id+"F0.wireOp",EDGE,"E157.MirrorCS")}),-1.0]])]});
            var Q5;
            Q5=makeQuery(id+"F0.imprint","IMPRINT",FACE,{"disambiguationData":[TD([[makeQuery(id+"F0.imprint","IMPRINT",EDGE,{"derivedFrom":sQuery(id+"F0.wireOp",EDGE,"E153.MirrorCS")}),-1.0]])]});
            var Q6;
            Q6=makeQuery(id+"F0.imprint","IMPRINT",FACE,{"disambiguationData":[TD([[makeQuery(id+"F0.imprint","IMPRINT",EDGE,{"derivedFrom":sQuery(id+"F0.wireOp",EDGE,"E216")}),1.0]])]});
            var Q7;
            {var subQ1=sQuery(id+"F0.wireOp",EDGE,"E90");Q7=makeQuery(id+"F0.imprint","IMPRINT",FACE,{"disambiguationData":[TD([[makeQuery(id+"F0.imprint","IMPRINT",EDGE,{"derivedFrom":subQ1}),1.0]])]});}
            var Q8;
            Q8=makeQuery(id+"F0.imprint","IMPRINT",FACE,{"disambiguationData":[TD([[makeQuery(id+"F0.imprint","IMPRINT",EDGE,{"derivedFrom":sQuery(id+"F0.wireOp",EDGE,"E82")}),1.0]])]});
            var Q9;
            {var subQ1=sQuery(id+"F0.wireOp",EDGE,"E50");Q9=makeQuery(id+"F0.imprint","IMPRINT",FACE,{"disambiguationData":[TD([[makeQuery(id+"F0.imprint","IMPRINT",EDGE,{"derivedFrom":subQ1}),1.0]])]});}
            var Q10;
            {var subQ1=sQuery(id+"F0.wireOp",EDGE,"E34");Q10=makeQuery(id+"F0.imprint","IMPRINT",FACE,{"disambiguationData":[TD([[makeQuery(id+"F0.imprint","IMPRINT",EDGE,{"derivedFrom":subQ1}),1.0]])]});}
            var Q11;
            {var subQ1=sQuery(id+"F0.wireOp",EDGE,"E26");Q11=makeQuery(id+"F0.imprint","IMPRINT",FACE,{"disambiguationData":[TD([[makeQuery(id+"F0.imprint","IMPRINT",EDGE,{"derivedFrom":subQ1}),1.0]])]});}
            var Q12;
            Q12=makeQuery(id+"F0.imprint","IMPRINT",FACE,{"disambiguationData":[TD([[makeQuery(id+"F0.imprint","IMPRINT",EDGE,{"derivedFrom":sQuery(id+"F0.wireOp",EDGE,"E18")}),1.0]])]});
            var Q13;
            {var subQ1=sQuery(id+"F0.wireOp",EDGE,"E10");Q13=makeQuery(id+"F0.imprint","IMPRINT",FACE,{"disambiguationData":[TD([[makeQuery(id+"F0.imprint","IMPRINT",EDGE,{"derivedFrom":subQ1}),1.0]])]});}
            var Q14;
            Q14=makeQuery(id+"F0.imprint","IMPRINT",FACE,{"disambiguationData":[TD([[makeQuery(id+"F0.imprint","IMPRINT",EDGE,{"derivedFrom":sQuery(id+"F0.wireOp",EDGE,"E2")}),1.0]])]});
            var Q15;
            Q15=makeQuery(id+"F0.imprint","IMPRINT",FACE,{"disambiguationData":[TD([[makeQuery(id+"F0.imprint","IMPRINT",EDGE,{"derivedFrom":sQuery(id+"F0.wireOp",EDGE,"E58")}),1.0]])]});
            var Q16;
            {var subQ1=sQuery(id+"F0.wireOp",EDGE,"E42");Q16=makeQuery(id+"F0.imprint","IMPRINT",FACE,{"disambiguationData":[TD([[makeQuery(id+"F0.imprint","IMPRINT",EDGE,{"derivedFrom":subQ1}),1.0]])]});}
            var Q17;
            Q17=makeQuery(id+"F0.imprint","IMPRINT",FACE,{"disambiguationData":[TD([[makeQuery(id+"F0.imprint","IMPRINT",EDGE,{"derivedFrom":sQuery(id+"F0.wireOp",EDGE,"E66")}),1.0]])]});
            var Q18;
            {var subQ1=sQuery(id+"F0.wireOp",EDGE,"E74");Q18=makeQuery(id+"F0.imprint","IMPRINT",FACE,{"disambiguationData":[TD([[makeQuery(id+"F0.imprint","IMPRINT",EDGE,{"derivedFrom":subQ1}),1.0]])]});}
            var Q19;
            {var subQ1=sQuery(id+"F0.wireOp",EDGE,"E208");Q19=makeQuery(id+"F0.imprint","IMPRINT",FACE,{"disambiguationData":[TD([[makeQuery(id+"F0.imprint","IMPRINT",EDGE,{"derivedFrom":subQ1}),1.0]])]});}
            var Q20;
            Q20=makeQuery(id+"F0.imprint","IMPRINT",FACE,{"disambiguationData":[TD([[makeQuery(id+"F0.imprint","IMPRINT",EDGE,{"derivedFrom":sQuery(id+"F0.wireOp",EDGE,"E110.MirrorCS")}),-1.0]])]});
            var Q21;
            Q21=makeQuery(id+"F0.imprint","IMPRINT",FACE,{"disambiguationData":[TD([[makeQuery(id+"F0.imprint","IMPRINT",EDGE,{"derivedFrom":sQuery(id+"F0.wireOp",EDGE,"E100.MirrorCS")}),-1.0]])]});
            var Q22;
            Q22=makeQuery(id+"F0.imprint","IMPRINT",FACE,{"disambiguationData":[TD([[makeQuery(id+"F0.imprint","IMPRINT",EDGE,{"derivedFrom":sQuery(id+"F0.wireOp",EDGE,"E98.MirrorCS")}),-1.0]])]});
            var Q23;
            Q23=makeQuery(id+"F0.imprint","IMPRINT",FACE,{"disambiguationData":[TD([[makeQuery(id+"F0.imprint","IMPRINT",EDGE,{"derivedFrom":sQuery(id+"F0.wireOp",EDGE,"E99.MirrorCS")}),-1.0]])]});
            var Q24;
            {var subQ1=sQuery(id+"F0.wireOp",EDGE,"E101.MirrorCS");Q24=makeQuery(id+"F0.imprint","IMPRINT",FACE,{"disambiguationData":[TD([[makeQuery(id+"F0.imprint","IMPRINT",EDGE,{"derivedFrom":subQ1}),-1.0]])]});}
            var Q25;
            Q25=makeQuery(id+"F0.imprint","IMPRINT",FACE,{"disambiguationData":[TD([[makeQuery(id+"F0.imprint","IMPRINT",EDGE,{"derivedFrom":sQuery(id+"F0.wireOp",EDGE,"E106.MirrorCS")}),-1.0]])]});
            var Q26;
            {var subQ0=sQuery(id+"F0.wireOp",EDGE,"E193.MirrorCS");Q26=makeQuery(id+"F0.imprint","IMPRINT",FACE,{"disambiguationData":[TD([[makeQuery(id+"F0.imprint","IMPRINT",EDGE,{"derivedFrom":subQ0}),-1.0]])]});}
            var Q27;
            {var subQ0=sQuery(id+"F0.wireOp",EDGE,"E172.MirrorCS");Q27=makeQuery(id+"F0.imprint","IMPRINT",FACE,{"disambiguationData":[TD([[makeQuery(id+"F0.imprint","IMPRINT",EDGE,{"derivedFrom":subQ0}),-1.0]])]});}
            var Q28;
            {var subQ0=sQuery(id+"F0.wireOp",EDGE,"E189.MirrorCS");Q28=makeQuery(id+"F0.imprint","IMPRINT",FACE,{"disambiguationData":[TD([[makeQuery(id+"F0.imprint","IMPRINT",EDGE,{"derivedFrom":subQ0}),-1.0]])]});}
            var Q29;
            {var subQ0=sQuery(id+"F0.wireOp",EDGE,"E185.MirrorCS");Q29=makeQuery(id+"F0.imprint","IMPRINT",FACE,{"disambiguationData":[TD([[makeQuery(id+"F0.imprint","IMPRINT",EDGE,{"derivedFrom":subQ0}),-1.0]])]});}
            var Q30;
            {var subQ0=sQuery(id+"F0.wireOp",EDGE,"E91");Q30=makeQuery(id+"F0.imprint","IMPRINT",FACE,{"disambiguationData":[TD([[makeQuery(id+"F0.imprint","IMPRINT",EDGE,{"derivedFrom":subQ0}),1.0]])]});}
            var Q31;
            {var subQ0=sQuery(id+"F0.wireOp",EDGE,"E35");Q31=makeQuery(id+"F0.imprint","IMPRINT",FACE,{"disambiguationData":[TD([[makeQuery(id+"F0.imprint","IMPRINT",EDGE,{"derivedFrom":subQ0}),1.0]])]});}
            var Q32;
            {var subQ0=sQuery(id+"F0.wireOp",EDGE,"E27");Q32=makeQuery(id+"F0.imprint","IMPRINT",FACE,{"disambiguationData":[TD([[makeQuery(id+"F0.imprint","IMPRINT",EDGE,{"derivedFrom":subQ0}),1.0]])]});}
            var Q33;
            {var subQ0=sQuery(id+"F0.wireOp",EDGE,"E11");Q33=makeQuery(id+"F0.imprint","IMPRINT",FACE,{"disambiguationData":[TD([[makeQuery(id+"F0.imprint","IMPRINT",EDGE,{"derivedFrom":subQ0}),1.0]])]});}
            var Q34;
            {var subQ0=sQuery(id+"F0.wireOp",EDGE,"E43");Q34=makeQuery(id+"F0.imprint","IMPRINT",FACE,{"disambiguationData":[TD([[makeQuery(id+"F0.imprint","IMPRINT",EDGE,{"derivedFrom":subQ0}),1.0]])]});}
            var Q35;
            {var subQ0=sQuery(id+"F0.wireOp",EDGE,"E103.MirrorCS");Q35=makeQuery(id+"F0.imprint","IMPRINT",FACE,{"disambiguationData":[TD([[makeQuery(id+"F0.imprint","IMPRINT",EDGE,{"derivedFrom":subQ0}),-1.0]])]});}
            var Q36;
            {var subQ0=sQuery(id+"F0.wireOp",EDGE,"E105.MirrorCS");Q36=makeQuery(id+"F0.imprint","IMPRINT",FACE,{"disambiguationData":[TD([[makeQuery(id+"F0.imprint","IMPRINT",EDGE,{"derivedFrom":subQ0}),-1.0]])]});}
            var Q37;
            {var subQ0=sQuery(id+"F0.wireOp",EDGE,"E102.MirrorCS");Q37=makeQuery(id+"F0.imprint","IMPRINT",FACE,{"disambiguationData":[TD([[makeQuery(id+"F0.imprint","IMPRINT",EDGE,{"derivedFrom":subQ0}),-1.0]])]});}
            var Q38;
            {var subQ0=sQuery(id+"F0.wireOp",EDGE,"E113.MirrorCS");Q38=makeQuery(id+"F0.imprint","IMPRINT",FACE,{"disambiguationData":[TD([[makeQuery(id+"F0.imprint","IMPRINT",EDGE,{"derivedFrom":subQ0}),-1.0]])]});}
            var Q39;
            {var subQ0=sQuery(id+"F0.wireOp",EDGE,"E138.MirrorCS");Q39=makeQuery(id+"F0.imprint","IMPRINT",FACE,{"disambiguationData":[TD([[makeQuery(id+"F0.imprint","IMPRINT",EDGE,{"derivedFrom":subQ0}),-1.0]])]});}
            var Q40;
            {var subQ5=sQuery(id+"F0.wireOp",EDGE,"E209");Q40=makeQuery(id+"F0.imprint","IMPRINT",FACE,{"disambiguationData":[TD([[makeQuery(id+"F0.imprint","IMPRINT",EDGE,{"derivedFrom":subQ5}),1.0]])]});}
            var Q41;
            {var subQ0=sQuery(id+"F0.wireOp",EDGE,"E75");Q41=makeQuery(id+"F0.imprint","IMPRINT",FACE,{"disambiguationData":[TD([[makeQuery(id+"F0.imprint","IMPRINT",EDGE,{"derivedFrom":subQ0}),1.0]])]});}
            var Q42;
            {var subQ0=sQuery(id+"F0.wireOp",EDGE,"E67");Q42=makeQuery(id+"F0.imprint","IMPRINT",FACE,{"disambiguationData":[TD([[makeQuery(id+"F0.imprint","IMPRINT",EDGE,{"derivedFrom":subQ0}),1.0]])]});}
            var Q43;
            {var subQ0=sQuery(id+"F0.wireOp",EDGE,"E59");Q43=makeQuery(id+"F0.imprint","IMPRINT",FACE,{"disambiguationData":[TD([[makeQuery(id+"F0.imprint","IMPRINT",EDGE,{"derivedFrom":subQ0}),1.0]])]});}
            var Q44;
            {var subQ0=sQuery(id+"F0.wireOp",EDGE,"E3");Q44=makeQuery(id+"F0.imprint","IMPRINT",FACE,{"disambiguationData":[TD([[makeQuery(id+"F0.imprint","IMPRINT",EDGE,{"derivedFrom":subQ0}),1.0]])]});}
            var Q45;
            {var subQ0=sQuery(id+"F0.wireOp",EDGE,"E19");Q45=makeQuery(id+"F0.imprint","IMPRINT",FACE,{"disambiguationData":[TD([[makeQuery(id+"F0.imprint","IMPRINT",EDGE,{"derivedFrom":subQ0}),1.0]])]});}
            var Q46;
            {var subQ0=sQuery(id+"F0.wireOp",EDGE,"E51");Q46=makeQuery(id+"F0.imprint","IMPRINT",FACE,{"disambiguationData":[TD([[makeQuery(id+"F0.imprint","IMPRINT",EDGE,{"derivedFrom":subQ0}),1.0]])]});}
            var Q47;
            {var subQ0=sQuery(id+"F0.wireOp",EDGE,"E217");Q47=makeQuery(id+"F0.imprint","IMPRINT",FACE,{"disambiguationData":[TD([[makeQuery(id+"F0.imprint","IMPRINT",EDGE,{"derivedFrom":subQ0}),1.0]])]});}
            var Q48;
            {var subQ0=sQuery(id+"F0.wireOp",EDGE,"E0");var subQ1=sQuery(id+"F0.wireOp",EDGE,"E184.MirrorCS");var subQ3=makeQuery(id+"F0.imprint","INTERSECT",VERTEX,{"derivedFrom":[subQ1,subQ0]});Q48=makeQuery(id+"F0.imprint","IMPRINT",FACE,{"disambiguationData":[TD([[makeQuery(id+"F0.imprint","IMPRINT",EDGE,{"disambiguationData":[TD([[subQ3,-1.0]])],"derivedFrom":subQ1}),-1.0]])]});}
            var Q49;
            {var subQ0=sQuery(id+"F0.wireOp",EDGE,"E0");var subQ1=sQuery(id+"F0.wireOp",EDGE,"E167.MirrorCS");var subQ3=makeQuery(id+"F0.imprint","INTERSECT",VERTEX,{"derivedFrom":[subQ1,subQ0]});Q49=makeQuery(id+"F0.imprint","IMPRINT",FACE,{"disambiguationData":[TD([[makeQuery(id+"F0.imprint","IMPRINT",EDGE,{"disambiguationData":[TD([[subQ3,-1.0]])],"derivedFrom":subQ1}),-1.0]])]});}
            var Q50;
            {var subQ1=sQuery(id+"F0.wireOp",EDGE,"E0");var subQ5=sQuery(id+"F0.wireOp",EDGE,"E207.MirrorCS");var subQ7=makeQuery(id+"F0.imprint","INTERSECT",VERTEX,{"derivedFrom":[subQ1,subQ5]});Q50=makeQuery(id+"F0.imprint","IMPRINT",FACE,{"disambiguationData":[TD([[makeQuery(id+"F0.imprint","IMPRINT",EDGE,{"disambiguationData":[TD([[subQ7,1.0]])],"derivedFrom":subQ1}),-1.0]])]});}
            var Q51;
            {var subQ0=sQuery(id+"F0.wireOp",EDGE,"E132.MirrorCS");Q51=makeQuery(id+"F0.imprint","IMPRINT",FACE,{"disambiguationData":[TD([[makeQuery(id+"F0.imprint","IMPRINT",EDGE,{"derivedFrom":subQ0}),-1.0]])]});}
            var Q52;
            Q52=makeQuery(id+"F0.imprint","IMPRINT",FACE,{"disambiguationData":[TD([[makeQuery(id+"F0.imprint","IMPRINT",EDGE,{"derivedFrom":sQuery(id+"F0.wireOp",EDGE,"E1")}),-1.0]])]});
            var Q53;
            {var subQ0=sQuery(id+"F0.wireOp",EDGE,"E83");Q53=makeQuery(id+"F0.imprint","IMPRINT",FACE,{"disambiguationData":[TD([[makeQuery(id+"F0.imprint","IMPRINT",EDGE,{"derivedFrom":subQ0}),1.0]])]});}
            extrude(context, id + "F2", {"entities" : qUnion([Q0, Q1, Q2, Q3, Q4, Q5, Q6, Q7, Q8, Q9, Q10, Q11, Q12, Q13, Q14, Q15, Q16, Q17, Q18, Q19, Q20, Q21, Q22, Q23, Q24, Q25, Q26, Q27, Q28, Q29, Q30, Q31, Q32, Q33, Q34, Q35, Q36, Q37, Q38, Q39, Q40, Q41, Q42, Q43, Q44, Q45, Q46, Q47, Q48, Q49, Q50, Q51, Q52, Q53]), "oppositeDirection" : true, "depth" : 25.4 * mm});
        }
        {
            var Q0;
            {var subQ5=sQuery(id+"F1.wireOp",EDGE,"E332");Q0=makeQuery(id+"F1.imprint","IMPRINT",FACE,{"disambiguationData":[TD([[makeQuery(id+"F1.imprint","IMPRINT",EDGE,{"derivedFrom":subQ5}),1.0]])]});}
            var Q1;
            {var subQ0=sQuery(id+"F1.wireOp",EDGE,"E259");Q1=makeQuery(id+"F1.imprint","IMPRINT",FACE,{"disambiguationData":[TD([[makeQuery(id+"F1.imprint","IMPRINT",EDGE,{"derivedFrom":subQ0}),1.0]])]});}
            var Q2;
            {var subQ1=sQuery(id+"F1.wireOp",EDGE,"E276.MirrorCS");Q2=makeQuery(id+"F1.imprint","IMPRINT",FACE,{"disambiguationData":[TD([[makeQuery(id+"F1.imprint","IMPRINT",EDGE,{"derivedFrom":subQ1}),1.0]])]});}
            var Q3;
            {var subQ2=sQuery(id+"F1.wireOp",EDGE,"E234");Q3=makeQuery(id+"F1.imprint","IMPRINT",FACE,{"disambiguationData":[TD([[makeQuery(id+"F1.imprint","IMPRINT",EDGE,{"derivedFrom":subQ2}),1.0]])]});}
            var Q4;
            {var subQ1=sQuery(id+"F1.wireOp",EDGE,"E226");Q4=makeQuery(id+"F1.imprint","IMPRINT",FACE,{"disambiguationData":[TD([[makeQuery(id+"F1.imprint","IMPRINT",EDGE,{"derivedFrom":subQ1}),1.0]])]});}
            var Q5;
            {var subQ2=sQuery(id+"F1.wireOp",EDGE,"E250");Q5=makeQuery(id+"F1.imprint","IMPRINT",FACE,{"disambiguationData":[TD([[makeQuery(id+"F1.imprint","IMPRINT",EDGE,{"derivedFrom":subQ2}),1.0]])]});}
            var Q6;
            Q6=makeQuery(id+"F1.imprint","IMPRINT",FACE,{"disambiguationData":[TD([[makeQuery(id+"F1.imprint","IMPRINT",EDGE,{"derivedFrom":sQuery(id+"F1.wireOp",EDGE,"E283.MirrorCS")}),-1.0]])]});
            var Q7;
            Q7=makeQuery(id+"F1.imprint","IMPRINT",FACE,{"disambiguationData":[TD([[makeQuery(id+"F1.imprint","IMPRINT",EDGE,{"derivedFrom":sQuery(id+"F1.wireOp",EDGE,"E293.MirrorCS")}),-1.0]])]});
            var Q8;
            {var subQ1=sQuery(id+"F1.wireOp",EDGE,"E347");Q8=makeQuery(id+"F1.imprint","IMPRINT",FACE,{"disambiguationData":[TD([[makeQuery(id+"F1.imprint","IMPRINT",EDGE,{"derivedFrom":subQ1}),1.0]])]});}
            var Q9;
            {var subQ0=sQuery(id+"F1.wireOp",EDGE,"E339");Q9=makeQuery(id+"F1.imprint","IMPRINT",FACE,{"disambiguationData":[TD([[makeQuery(id+"F1.imprint","IMPRINT",EDGE,{"derivedFrom":subQ0}),1.0]])]});}
            var Q10;
            {var subQ0=sQuery(id+"F1.wireOp",EDGE,"E323.MirrorC");var subQ1=sQuery(id+"F1.wireOp",EDGE,"E290.MirrorCS");var subQ2=makeQuery(id+"F1.imprint","INTERSECT",VERTEX,{"derivedFrom":[subQ1,subQ0]});Q10=makeQuery(id+"F1.imprint","IMPRINT",FACE,{"disambiguationData":[TD([[makeQuery(id+"F1.imprint","IMPRINT",EDGE,{"disambiguationData":[TD([[subQ2,1.0]])],"derivedFrom":subQ1}),1.0]])]});}
            var Q11;
            {var subQ1=sQuery(id+"F1.wireOp",EDGE,"E258");Q11=makeQuery(id+"F1.imprint","IMPRINT",FACE,{"disambiguationData":[TD([[makeQuery(id+"F1.imprint","IMPRINT",EDGE,{"derivedFrom":subQ1}),1.0]])]});}
            var Q12;
            Q12=makeQuery(id+"F1.imprint","IMPRINT",FACE,{"disambiguationData":[TD([[makeQuery(id+"F1.imprint","IMPRINT",EDGE,{"derivedFrom":sQuery(id+"F1.wireOp",EDGE,"E320.MirrorCS")}),-1.0]])]});
            var Q13;
            Q13=makeQuery(id+"F1.imprint","IMPRINT",FACE,{"disambiguationData":[TD([[makeQuery(id+"F1.imprint","IMPRINT",EDGE,{"derivedFrom":sQuery(id+"F1.wireOp",EDGE,"E294.MirrorCS")}),-1.0]])]});
            var Q14;
            {var subQ1=sQuery(id+"F1.wireOp",EDGE,"E331");Q14=makeQuery(id+"F1.imprint","IMPRINT",FACE,{"disambiguationData":[TD([[makeQuery(id+"F1.imprint","IMPRINT",EDGE,{"derivedFrom":subQ1}),1.0]])]});}
            var Q15;
            {var subQ1=sQuery(id+"F1.wireOp",EDGE,"E266");Q15=makeQuery(id+"F1.imprint","IMPRINT",FACE,{"disambiguationData":[TD([[makeQuery(id+"F1.imprint","IMPRINT",EDGE,{"derivedFrom":subQ1}),1.0]])]});}
            var Q16;
            Q16=makeQuery(id+"F1.imprint","IMPRINT",FACE,{"disambiguationData":[TD([[makeQuery(id+"F1.imprint","IMPRINT",EDGE,{"derivedFrom":sQuery(id+"F1.wireOp",EDGE,"E225")}),-1.0]])]});
            var Q17;
            {var subQ1=sQuery(id+"F1.wireOp",EDGE,"E242");Q17=makeQuery(id+"F1.imprint","IMPRINT",FACE,{"disambiguationData":[TD([[makeQuery(id+"F1.imprint","IMPRINT",EDGE,{"derivedFrom":subQ1}),1.0]])]});}
            var Q18;
            {var subQ1=sQuery(id+"F1.wireOp",EDGE,"E340");Q18=makeQuery(id+"F1.imprint","IMPRINT",FACE,{"disambiguationData":[TD([[makeQuery(id+"F1.imprint","IMPRINT",EDGE,{"derivedFrom":subQ1}),1.0]])]});}
            var Q19;
            Q19=makeQuery(id+"F1.imprint","IMPRINT",FACE,{"disambiguationData":[TD([[makeQuery(id+"F1.imprint","IMPRINT",EDGE,{"derivedFrom":sQuery(id+"F1.wireOp",EDGE,"E324.MirrorCS")}),-1.0]])]});
            var Q20;
            {var subQ5=sQuery(id+"F1.wireOp",EDGE,"E348");Q20=makeQuery(id+"F1.imprint","IMPRINT",FACE,{"disambiguationData":[TD([[makeQuery(id+"F1.imprint","IMPRINT",EDGE,{"derivedFrom":subQ5}),1.0]])]});}
            var Q21;
            {var subQ0=sQuery(id+"F1.wireOp",EDGE,"E267");Q21=makeQuery(id+"F1.imprint","IMPRINT",FACE,{"disambiguationData":[TD([[makeQuery(id+"F1.imprint","IMPRINT",EDGE,{"derivedFrom":subQ0}),1.0]])]});}
            var Q22;
            {var subQ0=sQuery(id+"F1.wireOp",EDGE,"E227");Q22=makeQuery(id+"F1.imprint","IMPRINT",FACE,{"disambiguationData":[TD([[makeQuery(id+"F1.imprint","IMPRINT",EDGE,{"derivedFrom":subQ0}),1.0]])]});}
            var Q23;
            {var subQ0=sQuery(id+"F1.wireOp",EDGE,"E282.MirrorCS");Q23=makeQuery(id+"F1.imprint","IMPRINT",FACE,{"disambiguationData":[TD([[makeQuery(id+"F1.imprint","IMPRINT",EDGE,{"derivedFrom":subQ0}),-1.0]])]});}
            var Q24;
            {var subQ0=sQuery(id+"F1.wireOp",EDGE,"E323.MirrorC");var subQ1=sQuery(id+"F1.wireOp",EDGE,"E306.MirrorCS");var subQ2=makeQuery(id+"F1.imprint","INTERSECT",VERTEX,{"derivedFrom":[subQ1,subQ0]});Q24=makeQuery(id+"F1.imprint","IMPRINT",FACE,{"disambiguationData":[TD([[makeQuery(id+"F1.imprint","IMPRINT",EDGE,{"disambiguationData":[TD([[subQ2,-1.0]])],"derivedFrom":subQ1}),1.0]])]});}
            var Q25;
            {var subQ0=sQuery(id+"F1.wireOp",EDGE,"E287.MirrorCS");Q25=makeQuery(id+"F1.imprint","IMPRINT",FACE,{"disambiguationData":[TD([[makeQuery(id+"F1.imprint","IMPRINT",EDGE,{"derivedFrom":subQ0}),1.0]])]});}
            var Q26;
            {var subQ0=sQuery(id+"F1.wireOp",EDGE,"E243");Q26=makeQuery(id+"F1.imprint","IMPRINT",FACE,{"disambiguationData":[TD([[makeQuery(id+"F1.imprint","IMPRINT",EDGE,{"derivedFrom":subQ0}),1.0]])]});}
            var Q27;
            {var subQ0=sQuery(id+"F1.wireOp",EDGE,"E352.filletArc");var subQ1=sQuery(id+"F1.wireOp",EDGE,"E224");var subQ2=makeQuery(id+"F1.imprint","INTERSECT",VERTEX,{"derivedFrom":[subQ1,subQ0]});Q27=makeQuery(id+"F1.imprint","IMPRINT",FACE,{"disambiguationData":[TD([[makeQuery(id+"F1.imprint","IMPRINT",EDGE,{"disambiguationData":[TD([[subQ2,-1.0]])],"derivedFrom":subQ1}),-1.0]])]});}
            var Q28;
            {var subQ0=sQuery(id+"F1.wireOp",EDGE,"E296.MirrorCS");Q28=makeQuery(id+"F1.imprint","IMPRINT",FACE,{"disambiguationData":[TD([[makeQuery(id+"F1.imprint","IMPRINT",EDGE,{"derivedFrom":subQ0}),-1.0]])]});}
            var Q29;
            {var subQ0=sQuery(id+"F1.wireOp",EDGE,"E305.MirrorCS");Q29=makeQuery(id+"F1.imprint","IMPRINT",FACE,{"disambiguationData":[TD([[makeQuery(id+"F1.imprint","IMPRINT",EDGE,{"derivedFrom":subQ0}),-1.0]])]});}
            var Q30;
            {var subQ0=sQuery(id+"F1.wireOp",EDGE,"E323.MirrorC");var subQ1=sQuery(id+"F1.wireOp",EDGE,"E288.MirrorCS");var subQ2=makeQuery(id+"F1.imprint","INTERSECT",VERTEX,{"derivedFrom":[subQ1,subQ0]});Q30=makeQuery(id+"F1.imprint","IMPRINT",FACE,{"disambiguationData":[TD([[makeQuery(id+"F1.imprint","IMPRINT",EDGE,{"disambiguationData":[TD([[subQ2,-1.0]])],"derivedFrom":subQ1}),-1.0]])]});}
            var Q31;
            {var subQ0=sQuery(id+"F1.wireOp",EDGE,"E238.filletArc");var subQ1=sQuery(id+"F1.wireOp",EDGE,"E235");var subQ2=makeQuery(id+"F1.imprint","INTERSECT",VERTEX,{"derivedFrom":[subQ1,subQ0]});Q31=makeQuery(id+"F1.imprint","IMPRINT",FACE,{"disambiguationData":[TD([[makeQuery(id+"F1.imprint","IMPRINT",EDGE,{"disambiguationData":[TD([[subQ2,-1.0]])],"derivedFrom":subQ1}),1.0]])]});}
            var Q32;
            {var subQ0=sQuery(id+"F1.wireOp",EDGE,"E323.MirrorC");var subQ1=sQuery(id+"F1.wireOp",EDGE,"E317.MirrorCS");var subQ2=makeQuery(id+"F1.imprint","INTERSECT",VERTEX,{"derivedFrom":[subQ1,subQ0]});Q32=makeQuery(id+"F1.imprint","IMPRINT",FACE,{"disambiguationData":[TD([[makeQuery(id+"F1.imprint","IMPRINT",EDGE,{"disambiguationData":[TD([[subQ2,-1.0]])],"derivedFrom":subQ1}),1.0]])]});}
            var Q33;
            {var subQ0=sQuery(id+"F1.wireOp",EDGE,"E323.MirrorC");var subQ1=sQuery(id+"F1.wireOp",EDGE,"E224");var subQ2=makeQuery(id+"F1.imprint","INTERSECT",VERTEX,{"disambiguationData":[OD(0.0)],"derivedFrom":[subQ1,subQ0]});Q33=makeQuery(id+"F1.imprint","IMPRINT",FACE,{"disambiguationData":[TD([[makeQuery(id+"F1.imprint","IMPRINT",EDGE,{"disambiguationData":[TD([[subQ2,-1.0]])],"derivedFrom":subQ1}),-1.0]])]});}
            var Q34;
            {var subQ0=sQuery(id+"F1.wireOp",EDGE,"E224");var subQ1=sQuery(id+"F1.wireOp",EDGE,"E246.filletArc");var subQ2=makeQuery(id+"F1.imprint","INTERSECT",VERTEX,{"derivedFrom":[subQ1,subQ0]});Q34=makeQuery(id+"F1.imprint","IMPRINT",FACE,{"disambiguationData":[TD([[makeQuery(id+"F1.imprint","IMPRINT",EDGE,{"disambiguationData":[TD([[subQ2,-1.0]])],"derivedFrom":subQ1}),-1.0]])]});}
            var Q35;
            {var subQ0=sQuery(id+"F1.wireOp",EDGE,"E224");var subQ1=sQuery(id+"F1.wireOp",EDGE,"E270.filletArc");var subQ2=makeQuery(id+"F1.imprint","INTERSECT",VERTEX,{"derivedFrom":[subQ1,subQ0]});Q35=makeQuery(id+"F1.imprint","IMPRINT",FACE,{"disambiguationData":[TD([[makeQuery(id+"F1.imprint","IMPRINT",EDGE,{"disambiguationData":[TD([[subQ2,-1.0]])],"derivedFrom":subQ1}),1.0]])]});}
            var Q36;
            {var subQ0=sQuery(id+"F1.wireOp",EDGE,"E254.filletArc");var subQ1=sQuery(id+"F1.wireOp",EDGE,"E251");var subQ2=makeQuery(id+"F1.imprint","INTERSECT",VERTEX,{"derivedFrom":[subQ1,subQ0]});Q36=makeQuery(id+"F1.imprint","IMPRINT",FACE,{"disambiguationData":[TD([[makeQuery(id+"F1.imprint","IMPRINT",EDGE,{"disambiguationData":[TD([[subQ2,-1.0]])],"derivedFrom":subQ1}),1.0]])]});}
            var Q37;
            {var subQ0=sQuery(id+"F1.wireOp",EDGE,"E343.filletArc");var subQ1=sQuery(id+"F1.wireOp",EDGE,"E224");var subQ2=makeQuery(id+"F1.imprint","INTERSECT",VERTEX,{"derivedFrom":[subQ1,subQ0]});Q37=makeQuery(id+"F1.imprint","IMPRINT",FACE,{"disambiguationData":[TD([[makeQuery(id+"F1.imprint","IMPRINT",EDGE,{"disambiguationData":[TD([[subQ2,1.0]])],"derivedFrom":subQ1}),1.0]])]});}
            var Q38;
            {var subQ1=sQuery(id+"F1.wireOp",EDGE,"E317.MirrorCS");var subQ7=sQuery(id+"F1.wireOp",EDGE,"E323.MirrorC");var subQ8=makeQuery(id+"F1.imprint","INTERSECT",VERTEX,{"derivedFrom":[subQ1,subQ7]});Q38=makeQuery(id+"F1.imprint","IMPRINT",FACE,{"disambiguationData":[TD([[makeQuery(id+"F1.imprint","IMPRINT",EDGE,{"disambiguationData":[TD([[subQ8,-1.0]])],"derivedFrom":subQ1}),-1.0]])]});}
            var Q39;
            {var subQ0=sQuery(id+"F1.wireOp",EDGE,"E323.MirrorC");var subQ1=sQuery(id+"F1.wireOp",EDGE,"E280.MirrorCS");var subQ2=makeQuery(id+"F1.imprint","INTERSECT",VERTEX,{"derivedFrom":[subQ1,subQ0]});Q39=makeQuery(id+"F1.imprint","IMPRINT",FACE,{"disambiguationData":[TD([[makeQuery(id+"F1.imprint","IMPRINT",EDGE,{"disambiguationData":[TD([[subQ2,1.0]])],"derivedFrom":subQ1}),-1.0]])]});}
            var Q40;
            {var subQ0=sQuery(id+"F1.wireOp",EDGE,"E323.MirrorC");var subQ1=sQuery(id+"F1.wireOp",EDGE,"E291.MirrorCS");var subQ2=makeQuery(id+"F1.imprint","INTERSECT",VERTEX,{"derivedFrom":[subQ1,subQ0]});Q40=makeQuery(id+"F1.imprint","IMPRINT",FACE,{"disambiguationData":[TD([[makeQuery(id+"F1.imprint","IMPRINT",EDGE,{"disambiguationData":[TD([[subQ2,-1.0]])],"derivedFrom":subQ1}),1.0]])]});}
            var Q41;
            {var subQ0=sQuery(id+"F1.wireOp",EDGE,"E336.filletArc");var subQ1=sQuery(id+"F1.wireOp",EDGE,"E224");var subQ2=makeQuery(id+"F1.imprint","INTERSECT",VERTEX,{"derivedFrom":[subQ1,subQ0]});Q41=makeQuery(id+"F1.imprint","IMPRINT",FACE,{"disambiguationData":[TD([[makeQuery(id+"F1.imprint","IMPRINT",EDGE,{"disambiguationData":[TD([[subQ2,-1.0]])],"derivedFrom":subQ1}),1.0]])]});}
            var Q42;
            {var subQ5=sQuery(id+"F1.wireOp",EDGE,"E325.MirrorCS");var subQ7=sQuery(id+"F1.wireOp",EDGE,"E327.MirrorCS");var subQ8=makeQuery(id+"F1.imprint","INTERSECT",VERTEX,{"derivedFrom":[subQ5,subQ7]});Q42=makeQuery(id+"F1.imprint","IMPRINT",FACE,{"disambiguationData":[TD([[makeQuery(id+"F1.imprint","IMPRINT",EDGE,{"disambiguationData":[TD([[subQ8,1.0]])],"derivedFrom":subQ5}),1.0]])]});}
            var Q43;
            {var subQ0=sQuery(id+"F1.wireOp",EDGE,"E335.filletArc");var subQ1=sQuery(id+"F1.wireOp",EDGE,"E224");var subQ2=makeQuery(id+"F1.imprint","INTERSECT",VERTEX,{"derivedFrom":[subQ1,subQ0]});Q43=makeQuery(id+"F1.imprint","IMPRINT",FACE,{"disambiguationData":[TD([[makeQuery(id+"F1.imprint","IMPRINT",EDGE,{"disambiguationData":[TD([[subQ2,-1.0]])],"derivedFrom":subQ1}),1.0]])]});}
            var Q44;
            {var subQ0=sQuery(id+"F1.wireOp",EDGE,"E224");var subQ1=sQuery(id+"F1.wireOp",EDGE,"E262.filletArc");var subQ2=makeQuery(id+"F1.imprint","INTERSECT",VERTEX,{"derivedFrom":[subQ1,subQ0]});Q44=makeQuery(id+"F1.imprint","IMPRINT",FACE,{"disambiguationData":[TD([[makeQuery(id+"F1.imprint","IMPRINT",EDGE,{"disambiguationData":[TD([[subQ2,-1.0]])],"derivedFrom":subQ1}),-1.0]])]});}
            var Q45;
            {var subQ0=sQuery(id+"F1.wireOp",EDGE,"E224");var subQ1=sQuery(id+"F1.wireOp",EDGE,"E262.filletArc");var subQ2=makeQuery(id+"F1.imprint","INTERSECT",VERTEX,{"derivedFrom":[subQ1,subQ0]});Q45=makeQuery(id+"F1.imprint","IMPRINT",FACE,{"disambiguationData":[TD([[makeQuery(id+"F1.imprint","IMPRINT",EDGE,{"disambiguationData":[TD([[subQ2,-1.0]])],"derivedFrom":subQ1}),1.0]])]});}
            var Q46;
            {var subQ0=sQuery(id+"F1.wireOp",EDGE,"E239.filletArc");var subQ1=sQuery(id+"F1.wireOp",EDGE,"E235");var subQ2=makeQuery(id+"F1.imprint","INTERSECT",VERTEX,{"derivedFrom":[subQ1,subQ0]});Q46=makeQuery(id+"F1.imprint","IMPRINT",FACE,{"disambiguationData":[TD([[makeQuery(id+"F1.imprint","IMPRINT",EDGE,{"disambiguationData":[TD([[subQ2,1.0]])],"derivedFrom":subQ1}),1.0]])]});}
            var Q47;
            {var subQ5=sQuery(id+"F1.wireOp",EDGE,"E304.MirrorCS");var subQ7=sQuery(id+"F1.wireOp",EDGE,"E297.MirrorCS");var subQ9=makeQuery(id+"F1.imprint","INTERSECT",VERTEX,{"derivedFrom":[subQ7,subQ5]});Q47=makeQuery(id+"F1.imprint","IMPRINT",FACE,{"disambiguationData":[TD([[makeQuery(id+"F1.imprint","IMPRINT",EDGE,{"disambiguationData":[TD([[subQ9,1.0]])],"derivedFrom":subQ7}),1.0]])]});}
            var Q48;
            {var subQ0=sQuery(id+"F1.wireOp",EDGE,"E323.MirrorC");var subQ1=sQuery(id+"F1.wireOp",EDGE,"E280.MirrorCS");var subQ2=makeQuery(id+"F1.imprint","INTERSECT",VERTEX,{"derivedFrom":[subQ1,subQ0]});Q48=makeQuery(id+"F1.imprint","IMPRINT",FACE,{"disambiguationData":[TD([[makeQuery(id+"F1.imprint","IMPRINT",EDGE,{"disambiguationData":[TD([[subQ2,1.0]])],"derivedFrom":subQ1}),1.0]])]});}
            var Q49;
            {var subQ0=sQuery(id+"F1.wireOp",EDGE,"E224");var subQ1=sQuery(id+"F1.wireOp",EDGE,"E230.filletArc");var subQ2=makeQuery(id+"F1.imprint","INTERSECT",VERTEX,{"derivedFrom":[subQ1,subQ0]});Q49=makeQuery(id+"F1.imprint","IMPRINT",FACE,{"disambiguationData":[TD([[makeQuery(id+"F1.imprint","IMPRINT",EDGE,{"disambiguationData":[TD([[subQ2,-1.0]])],"derivedFrom":subQ1}),1.0]])]});}
            var Q50;
            {var subQ0=sQuery(id+"F1.wireOp",EDGE,"E224");var subQ1=sQuery(id+"F1.wireOp",EDGE,"E230.filletArc");var subQ2=makeQuery(id+"F1.imprint","INTERSECT",VERTEX,{"derivedFrom":[subQ1,subQ0]});Q50=makeQuery(id+"F1.imprint","IMPRINT",FACE,{"disambiguationData":[TD([[makeQuery(id+"F1.imprint","IMPRINT",EDGE,{"disambiguationData":[TD([[subQ2,-1.0]])],"derivedFrom":subQ1}),-1.0]])]});}
            var Q51;
            {var subQ1=sQuery(id+"F1.wireOp",EDGE,"E239.filletArc");var subQ7=sQuery(id+"F1.wireOp",EDGE,"E235");var subQ8=makeQuery(id+"F1.imprint","INTERSECT",VERTEX,{"derivedFrom":[subQ7,subQ1]});Q51=makeQuery(id+"F1.imprint","IMPRINT",FACE,{"disambiguationData":[TD([[makeQuery(id+"F1.imprint","IMPRINT",EDGE,{"disambiguationData":[TD([[subQ8,1.0]])],"derivedFrom":subQ7}),-1.0]])]});}
            var Q52;
            {var subQ0=sQuery(id+"F1.wireOp",EDGE,"E323.MirrorC");var subQ1=sQuery(id+"F1.wireOp",EDGE,"E290.MirrorCS");var subQ2=makeQuery(id+"F1.imprint","INTERSECT",VERTEX,{"derivedFrom":[subQ1,subQ0]});Q52=makeQuery(id+"F1.imprint","IMPRINT",FACE,{"disambiguationData":[TD([[makeQuery(id+"F1.imprint","IMPRINT",EDGE,{"disambiguationData":[TD([[subQ2,1.0]])],"derivedFrom":subQ1}),-1.0]])]});}
            var Q53;
            {var subQ0=sQuery(id+"F1.wireOp",EDGE,"E224");var subQ1=sQuery(id+"F1.wireOp",EDGE,"E271.filletArc");var subQ2=makeQuery(id+"F1.imprint","INTERSECT",VERTEX,{"derivedFrom":[subQ1,subQ0]});Q53=makeQuery(id+"F1.imprint","IMPRINT",FACE,{"disambiguationData":[TD([[makeQuery(id+"F1.imprint","IMPRINT",EDGE,{"disambiguationData":[TD([[subQ2,1.0]])],"derivedFrom":subQ1}),-1.0]])]});}
            var Q54;
            {var subQ0=sQuery(id+"F1.wireOp",EDGE,"E224");var subQ1=sQuery(id+"F1.wireOp",EDGE,"E231.filletArc");var subQ2=makeQuery(id+"F1.imprint","INTERSECT",VERTEX,{"derivedFrom":[subQ1,subQ0]});Q54=makeQuery(id+"F1.imprint","IMPRINT",FACE,{"disambiguationData":[TD([[makeQuery(id+"F1.imprint","IMPRINT",EDGE,{"disambiguationData":[TD([[subQ2,1.0]])],"derivedFrom":subQ1}),-1.0]])]});}
            var Q55;
            {var subQ1=sQuery(id+"F1.wireOp",EDGE,"E255.filletArc");var subQ7=sQuery(id+"F1.wireOp",EDGE,"E251");var subQ8=makeQuery(id+"F1.imprint","INTERSECT",VERTEX,{"derivedFrom":[subQ7,subQ1]});Q55=makeQuery(id+"F1.imprint","IMPRINT",FACE,{"disambiguationData":[TD([[makeQuery(id+"F1.imprint","IMPRINT",EDGE,{"disambiguationData":[TD([[subQ8,1.0]])],"derivedFrom":subQ7}),-1.0]])]});}
            var Q56;
            {var subQ0=sQuery(id+"F1.wireOp",EDGE,"E255.filletArc");var subQ1=sQuery(id+"F1.wireOp",EDGE,"E251");var subQ2=makeQuery(id+"F1.imprint","INTERSECT",VERTEX,{"derivedFrom":[subQ1,subQ0]});Q56=makeQuery(id+"F1.imprint","IMPRINT",FACE,{"disambiguationData":[TD([[makeQuery(id+"F1.imprint","IMPRINT",EDGE,{"disambiguationData":[TD([[subQ2,1.0]])],"derivedFrom":subQ1}),1.0]])]});}
            var Q57;
            {var subQ0=sQuery(id+"F1.wireOp",EDGE,"E323.MirrorC");var subQ1=sQuery(id+"F1.wireOp",EDGE,"E306.MirrorCS");var subQ2=makeQuery(id+"F1.imprint","INTERSECT",VERTEX,{"derivedFrom":[subQ1,subQ0]});Q57=makeQuery(id+"F1.imprint","IMPRINT",FACE,{"disambiguationData":[TD([[makeQuery(id+"F1.imprint","IMPRINT",EDGE,{"disambiguationData":[TD([[subQ2,-1.0]])],"derivedFrom":subQ1}),-1.0]])]});}
            var Q58;
            {var subQ1=sQuery(id+"F1.wireOp",EDGE,"E327.MirrorCS");var subQ6=sQuery(id+"F1.wireOp",EDGE,"E325.MirrorCS");var subQ9=makeQuery(id+"F1.imprint","INTERSECT",VERTEX,{"derivedFrom":[subQ6,subQ1]});Q58=makeQuery(id+"F1.imprint","IMPRINT",FACE,{"disambiguationData":[TD([[makeQuery(id+"F1.imprint","IMPRINT",EDGE,{"disambiguationData":[TD([[subQ9,1.0]])],"derivedFrom":subQ6}),-1.0]])]});}
            var Q59;
            {var subQ0=sQuery(id+"F1.wireOp",EDGE,"E323.MirrorC");var subQ1=sQuery(id+"F1.wireOp",EDGE,"E224");var subQ2=makeQuery(id+"F1.imprint","INTERSECT",VERTEX,{"disambiguationData":[OD(1.0)],"derivedFrom":[subQ1,subQ0]});Q59=makeQuery(id+"F1.imprint","IMPRINT",FACE,{"disambiguationData":[TD([[makeQuery(id+"F1.imprint","IMPRINT",EDGE,{"disambiguationData":[TD([[subQ2,1.0]])],"derivedFrom":subQ1}),-1.0]])]});}
            var Q60;
            {var subQ0=sQuery(id+"F1.wireOp",EDGE,"E224");var subQ1=sQuery(id+"F1.wireOp",EDGE,"E246.filletArc");var subQ2=makeQuery(id+"F1.imprint","INTERSECT",VERTEX,{"derivedFrom":[subQ1,subQ0]});Q60=makeQuery(id+"F1.imprint","IMPRINT",FACE,{"disambiguationData":[TD([[makeQuery(id+"F1.imprint","IMPRINT",EDGE,{"disambiguationData":[TD([[subQ2,-1.0]])],"derivedFrom":subQ1}),1.0]])]});}
            var Q61;
            {var subQ0=sQuery(id+"F1.wireOp",EDGE,"E291.MirrorCS");var subQ1=sQuery(id+"F1.wireOp",EDGE,"E290.MirrorCS");var subQ2=makeQuery(id+"F1.imprint","INTERSECT",VERTEX,{"derivedFrom":[subQ1,subQ0]});Q61=makeQuery(id+"F1.imprint","IMPRINT",FACE,{"disambiguationData":[TD([[makeQuery(id+"F1.imprint","IMPRINT",EDGE,{"disambiguationData":[TD([[subQ2,-1.0]])],"derivedFrom":subQ1}),-1.0]])]});}
            var Q62;
            {var subQ0=sQuery(id+"F1.wireOp",EDGE,"E318.MirrorCS");var subQ1=sQuery(id+"F1.wireOp",EDGE,"E325.MirrorCS");var subQ2=makeQuery(id+"F1.imprint","INTERSECT",VERTEX,{"derivedFrom":[subQ1,subQ0]});Q62=makeQuery(id+"F1.imprint","IMPRINT",FACE,{"disambiguationData":[TD([[makeQuery(id+"F1.imprint","IMPRINT",EDGE,{"disambiguationData":[TD([[subQ2,-1.0]])],"derivedFrom":subQ1}),-1.0]])]});}
            var Q63;
            {var subQ0=sQuery(id+"F1.wireOp",EDGE,"E297.MirrorCS");var subQ1=sQuery(id+"F1.wireOp",EDGE,"E317.MirrorCS");var subQ2=makeQuery(id+"F1.imprint","INTERSECT",VERTEX,{"derivedFrom":[subQ1,subQ0]});Q63=makeQuery(id+"F1.imprint","IMPRINT",FACE,{"disambiguationData":[TD([[makeQuery(id+"F1.imprint","IMPRINT",EDGE,{"disambiguationData":[TD([[subQ2,1.0]])],"derivedFrom":subQ1}),-1.0]])]});}
            extrude(context, id + "F3", {"entities" : qUnion([Q0, Q1, Q2, Q3, Q4, Q5, Q6, Q7, Q8, Q9, Q10, Q11, Q12, Q13, Q14, Q15, Q16, Q17, Q18, Q19, Q20, Q21, Q22, Q23, Q24, Q25, Q26, Q27, Q28, Q29, Q30, Q31, Q32, Q33, Q34, Q35, Q36, Q37, Q38, Q39, Q40, Q41, Q42, Q43, Q44, Q45, Q46, Q47, Q48, Q49, Q50, Q51, Q52, Q53, Q54, Q55, Q56, Q57, Q58, Q59, Q60, Q61, Q62, Q63]), "depth" : 6.35 * mm});
        }
    });
